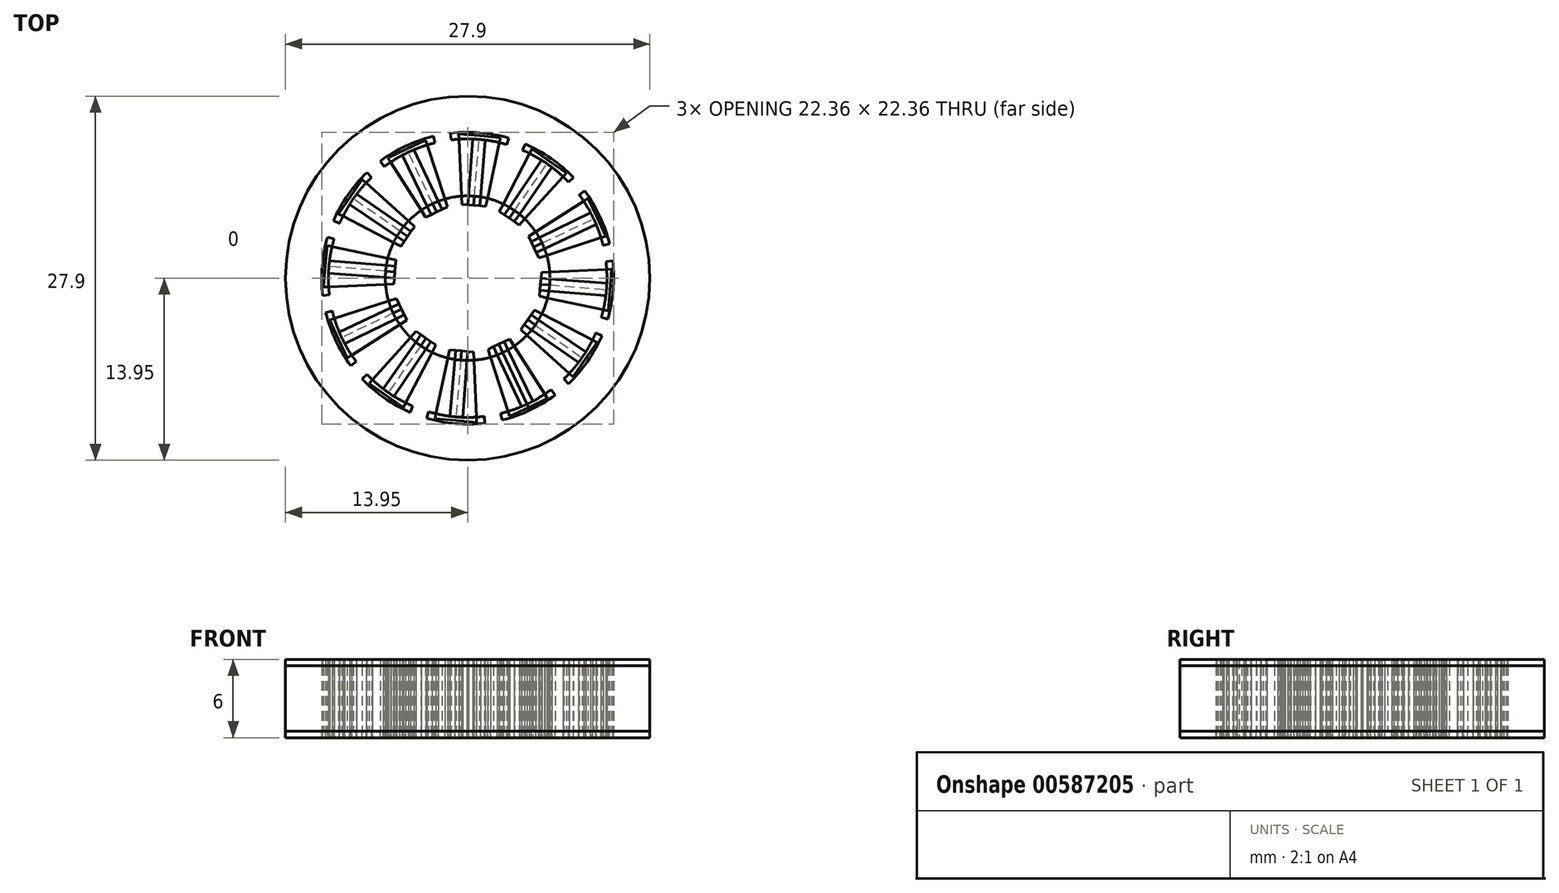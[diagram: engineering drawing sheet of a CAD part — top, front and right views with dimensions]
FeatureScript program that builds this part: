
annotation { "Feature Type Name" : "Feature", "Feature Type Description" : "" }
export const myFeature = defineFeature(function(context is Context, id is Id, definition is map)
    precondition{}
    {
        {
            var Q0;
            Q0=qCreatedBy(makeId("Top.planeOp"),FACE);
            var sketch = newSketch(context, id + "F0", { "sketchPlane" : qUnion([Q0])});
            skCircle(sketch, "E0", {"center": v(0, 0) * mm, "radius": 13.95 * mm});
            skCircle(sketch, "E1", {"center": v(0, 0) * mm, "radius": 4 * mm});
            skCircle(sketch, "E2", {"center": v(0, 0) * mm, "radius": 4.7 * mm});
            skCircle(sketch, "E3", {"center": v(0, 0) * mm, "radius": 6.3 * mm});
            skCircle(sketch, "E4", {"center": v(0, 0) * mm, "radius": 11.19 * mm, "construction": true});
            skCircle(sketch, "E5", {"center": v(0, 0) * mm, "radius": 10.67 * mm, "construction": true});
            skLineSegment(sketch, "E6", {"start": v(0, 0) * mm, "end": v(6.7, -8.96) * mm, "construction": true});
            skLineSegment(sketch, "E7", {"start": v(0, 0) * mm, "end": v(2.64, -10.87) * mm, "construction": true});
            skArc(sketch, "E8", {"start": v(2.52, -10.37) * mm, "mid": v(4.55, -9.65) * mm, "end": v(6.39, -8.54) * mm});
            skArc(sketch, "E9", {"start": v(2.64, -10.87) * mm, "mid": v(4.76, -10.11) * mm, "end": v(6.7, -8.96) * mm});
            skLineSegment(sketch, "E10", {"start": v(6.7, -8.96) * mm, "end": v(6.39, -8.54) * mm});
            skLineSegment(sketch, "E11", {"start": v(2.64, -10.87) * mm, "end": v(2.52, -10.37) * mm});
            skLineSegment(sketch, "E12", {"start": v(0, 0) * mm, "end": v(4.55, -9.65) * mm});
            skLineSegment(sketch, "E13", {"start": v(4.55, -9.65) * mm, "end": v(4.66, -9.9) * mm});
            skLineSegment(sketch, "E14", {"start": v(4.66, -9.9) * mm, "end": v(6.11, -9.22) * mm});
            skLineSegment(sketch, "E15", {"start": v(4.66, -9.9) * mm, "end": v(3.22, -10.58) * mm});
            skLineSegment(sketch, "E16", {"start": v(2.88, -6.12) * mm, "end": v(2.38, -5.06) * mm});
            skLineSegment(sketch, "E17", {"start": v(2.38, -5.06) * mm, "end": v(3.22, -4.67) * mm});
            skLineSegment(sketch, "E18", {"start": v(3.22, -4.67) * mm, "end": v(6.11, -9.22) * mm});
            skLineSegment(sketch, "E19", {"start": v(2.38, -5.06) * mm, "end": v(1.55, -5.45) * mm});
            skLineSegment(sketch, "E20", {"start": v(3.22, -10.58) * mm, "end": v(1.55, -5.45) * mm});
            skLineSegment(sketch, "E21.1.0", {"start": v(0, 0) * mm, "end": v(8.76, -6.08) * mm});
            skLineSegment(sketch, "E21.1.1", {"start": v(0, 0) * mm, "end": v(7.72, -8.1) * mm, "construction": true});
            skLineSegment(sketch, "E21.1.2", {"start": v(0, 0) * mm, "end": v(10.28, -4.4) * mm, "construction": true});
            skLineSegment(sketch, "E21.1.3", {"start": v(4.6, -3.2) * mm, "end": v(5.12, -2.43) * mm});
            skLineSegment(sketch, "E21.1.4", {"start": v(4.6, -3.2) * mm, "end": v(4.07, -3.95) * mm});
            skLineSegment(sketch, "E21.1.5", {"start": v(8.08, -7.56) * mm, "end": v(4.07, -3.95) * mm});
            skLineSegment(sketch, "E21.1.6", {"start": v(5.12, -2.43) * mm, "end": v(9.9, -4.93) * mm});
            skLineSegment(sketch, "E21.1.7", {"start": v(8.99, -6.24) * mm, "end": v(8.08, -7.56) * mm});
            skLineSegment(sketch, "E21.1.8", {"start": v(8.99, -6.24) * mm, "end": v(9.9, -4.93) * mm});
            skArc(sketch, "E21.1.9", {"start": v(7.36, -7.72) * mm, "mid": v(8.76, -6.08) * mm, "end": v(9.8, -4.2) * mm});
            skArc(sketch, "E21.1.10", {"start": v(7.72, -8.1) * mm, "mid": v(9.18, -6.38) * mm, "end": v(10.28, -4.4) * mm});
            skLineSegment(sketch, "E21.2.0", {"start": v(0, 0) * mm, "end": v(10.63, -0.89) * mm});
            skLineSegment(sketch, "E21.2.1", {"start": v(0, 0) * mm, "end": v(10.74, -3.15) * mm, "construction": true});
            skLineSegment(sketch, "E21.2.2", {"start": v(0, 0) * mm, "end": v(11.11, 1.32) * mm, "construction": true});
            skLineSegment(sketch, "E21.2.3", {"start": v(5.58, -0.47) * mm, "end": v(5.65, 0.45) * mm});
            skLineSegment(sketch, "E21.2.4", {"start": v(5.58, -0.47) * mm, "end": v(5.5, -1.38) * mm});
            skLineSegment(sketch, "E21.2.5", {"start": v(10.77, -2.5) * mm, "end": v(5.5, -1.38) * mm});
            skLineSegment(sketch, "E21.2.6", {"start": v(5.65, 0.45) * mm, "end": v(11.04, 0.68) * mm});
            skLineSegment(sketch, "E21.2.7", {"start": v(10.9, -0.91) * mm, "end": v(10.77, -2.5) * mm});
            skLineSegment(sketch, "E21.2.8", {"start": v(10.9, -0.91) * mm, "end": v(11.04, 0.68) * mm});
            skArc(sketch, "E21.2.9", {"start": v(10.24, -3) * mm, "mid": v(10.63, -0.89) * mm, "end": v(10.6, 1.26) * mm});
            skArc(sketch, "E21.2.10", {"start": v(10.74, -3.15) * mm, "mid": v(11.14, -0.93) * mm, "end": v(11.11, 1.32) * mm});
            skLineSegment(sketch, "E21.3.0", {"start": v(0, 0) * mm, "end": v(9.65, 4.55) * mm});
            skLineSegment(sketch, "E21.3.1", {"start": v(0, 0) * mm, "end": v(10.87, 2.64) * mm, "construction": true});
            skLineSegment(sketch, "E21.3.2", {"start": v(0, 0) * mm, "end": v(8.96, 6.7) * mm, "construction": true});
            skLineSegment(sketch, "E21.3.3", {"start": v(5.06, 2.38) * mm, "end": v(4.67, 3.22) * mm});
            skLineSegment(sketch, "E21.3.4", {"start": v(5.06, 2.38) * mm, "end": v(5.45, 1.55) * mm});
            skLineSegment(sketch, "E21.3.5", {"start": v(10.58, 3.22) * mm, "end": v(5.45, 1.55) * mm});
            skLineSegment(sketch, "E21.3.6", {"start": v(4.67, 3.22) * mm, "end": v(9.22, 6.11) * mm});
            skLineSegment(sketch, "E21.3.7", {"start": v(9.9, 4.66) * mm, "end": v(10.58, 3.22) * mm});
            skLineSegment(sketch, "E21.3.8", {"start": v(9.9, 4.66) * mm, "end": v(9.22, 6.11) * mm});
            skArc(sketch, "E21.3.9", {"start": v(10.37, 2.52) * mm, "mid": v(9.65, 4.55) * mm, "end": v(8.54, 6.39) * mm});
            skArc(sketch, "E21.3.10", {"start": v(10.87, 2.64) * mm, "mid": v(10.11, 4.76) * mm, "end": v(8.96, 6.7) * mm});
            skLineSegment(sketch, "E21.4.0", {"start": v(0, 0) * mm, "end": v(6.08, 8.76) * mm});
            skLineSegment(sketch, "E21.4.1", {"start": v(0, 0) * mm, "end": v(8.1, 7.72) * mm, "construction": true});
            skLineSegment(sketch, "E21.4.2", {"start": v(0, 0) * mm, "end": v(4.4, 10.28) * mm, "construction": true});
            skLineSegment(sketch, "E21.4.3", {"start": v(3.2, 4.6) * mm, "end": v(2.43, 5.12) * mm});
            skLineSegment(sketch, "E21.4.4", {"start": v(3.2, 4.6) * mm, "end": v(3.95, 4.07) * mm});
            skLineSegment(sketch, "E21.4.5", {"start": v(7.56, 8.08) * mm, "end": v(3.95, 4.07) * mm});
            skLineSegment(sketch, "E21.4.6", {"start": v(2.43, 5.12) * mm, "end": v(4.93, 9.9) * mm});
            skLineSegment(sketch, "E21.4.7", {"start": v(6.24, 8.99) * mm, "end": v(7.56, 8.08) * mm});
            skLineSegment(sketch, "E21.4.8", {"start": v(6.24, 8.99) * mm, "end": v(4.93, 9.9) * mm});
            skArc(sketch, "E21.4.9", {"start": v(7.72, 7.36) * mm, "mid": v(6.08, 8.76) * mm, "end": v(4.2, 9.8) * mm});
            skArc(sketch, "E21.4.10", {"start": v(8.1, 7.72) * mm, "mid": v(6.38, 9.18) * mm, "end": v(4.4, 10.28) * mm});
            skLineSegment(sketch, "E21.5.0", {"start": v(0, 0) * mm, "end": v(0.89, 10.63) * mm});
            skLineSegment(sketch, "E21.5.1", {"start": v(0, 0) * mm, "end": v(3.15, 10.74) * mm, "construction": true});
            skLineSegment(sketch, "E21.5.2", {"start": v(0, 0) * mm, "end": v(-1.32, 11.11) * mm, "construction": true});
            skLineSegment(sketch, "E21.5.3", {"start": v(0.47, 5.58) * mm, "end": v(-0.45, 5.65) * mm});
            skLineSegment(sketch, "E21.5.4", {"start": v(0.47, 5.58) * mm, "end": v(1.38, 5.5) * mm});
            skLineSegment(sketch, "E21.5.5", {"start": v(2.5, 10.77) * mm, "end": v(1.38, 5.5) * mm});
            skLineSegment(sketch, "E21.5.6", {"start": v(-0.45, 5.65) * mm, "end": v(-0.68, 11.04) * mm});
            skLineSegment(sketch, "E21.5.7", {"start": v(0.91, 10.9) * mm, "end": v(2.5, 10.77) * mm});
            skLineSegment(sketch, "E21.5.8", {"start": v(0.91, 10.9) * mm, "end": v(-0.68, 11.04) * mm});
            skArc(sketch, "E21.5.9", {"start": v(3, 10.24) * mm, "mid": v(0.89, 10.63) * mm, "end": v(-1.26, 10.6) * mm});
            skArc(sketch, "E21.5.10", {"start": v(3.15, 10.74) * mm, "mid": v(0.93, 11.14) * mm, "end": v(-1.32, 11.11) * mm});
            skLineSegment(sketch, "E21.6.0", {"start": v(0, 0) * mm, "end": v(-4.55, 9.65) * mm});
            skLineSegment(sketch, "E21.6.1", {"start": v(0, 0) * mm, "end": v(-2.64, 10.87) * mm, "construction": true});
            skLineSegment(sketch, "E21.6.2", {"start": v(0, 0) * mm, "end": v(-6.7, 8.96) * mm, "construction": true});
            skLineSegment(sketch, "E21.6.3", {"start": v(-2.38, 5.06) * mm, "end": v(-3.22, 4.67) * mm});
            skLineSegment(sketch, "E21.6.4", {"start": v(-2.38, 5.06) * mm, "end": v(-1.55, 5.45) * mm});
            skLineSegment(sketch, "E21.6.5", {"start": v(-3.22, 10.58) * mm, "end": v(-1.55, 5.45) * mm});
            skLineSegment(sketch, "E21.6.6", {"start": v(-3.22, 4.67) * mm, "end": v(-6.11, 9.22) * mm});
            skLineSegment(sketch, "E21.6.7", {"start": v(-4.66, 9.9) * mm, "end": v(-3.22, 10.58) * mm});
            skLineSegment(sketch, "E21.6.8", {"start": v(-4.66, 9.9) * mm, "end": v(-6.11, 9.22) * mm});
            skArc(sketch, "E21.6.9", {"start": v(-2.52, 10.37) * mm, "mid": v(-4.55, 9.65) * mm, "end": v(-6.39, 8.54) * mm});
            skArc(sketch, "E21.6.10", {"start": v(-2.64, 10.87) * mm, "mid": v(-4.76, 10.11) * mm, "end": v(-6.7, 8.96) * mm});
            skLineSegment(sketch, "E21.7.0", {"start": v(0, 0) * mm, "end": v(-8.76, 6.08) * mm});
            skLineSegment(sketch, "E21.7.1", {"start": v(0, 0) * mm, "end": v(-7.72, 8.1) * mm, "construction": true});
            skLineSegment(sketch, "E21.7.2", {"start": v(0, 0) * mm, "end": v(-10.28, 4.4) * mm, "construction": true});
            skLineSegment(sketch, "E21.7.3", {"start": v(-4.6, 3.2) * mm, "end": v(-5.12, 2.43) * mm});
            skLineSegment(sketch, "E21.7.4", {"start": v(-4.6, 3.2) * mm, "end": v(-4.07, 3.95) * mm});
            skLineSegment(sketch, "E21.7.5", {"start": v(-8.08, 7.56) * mm, "end": v(-4.07, 3.95) * mm});
            skLineSegment(sketch, "E21.7.6", {"start": v(-5.12, 2.43) * mm, "end": v(-9.9, 4.93) * mm});
            skLineSegment(sketch, "E21.7.7", {"start": v(-8.99, 6.24) * mm, "end": v(-8.08, 7.56) * mm});
            skLineSegment(sketch, "E21.7.8", {"start": v(-8.99, 6.24) * mm, "end": v(-9.9, 4.93) * mm});
            skArc(sketch, "E21.7.9", {"start": v(-7.36, 7.72) * mm, "mid": v(-8.76, 6.08) * mm, "end": v(-9.8, 4.2) * mm});
            skArc(sketch, "E21.7.10", {"start": v(-7.72, 8.1) * mm, "mid": v(-9.18, 6.38) * mm, "end": v(-10.28, 4.4) * mm});
            skLineSegment(sketch, "E21.8.0", {"start": v(0, 0) * mm, "end": v(-10.63, 0.89) * mm});
            skLineSegment(sketch, "E21.8.1", {"start": v(0, 0) * mm, "end": v(-10.74, 3.15) * mm, "construction": true});
            skLineSegment(sketch, "E21.8.2", {"start": v(0, 0) * mm, "end": v(-11.11, -1.32) * mm, "construction": true});
            skLineSegment(sketch, "E21.8.3", {"start": v(-5.58, 0.47) * mm, "end": v(-5.65, -0.45) * mm});
            skLineSegment(sketch, "E21.8.4", {"start": v(-5.58, 0.47) * mm, "end": v(-5.5, 1.38) * mm});
            skLineSegment(sketch, "E21.8.5", {"start": v(-10.77, 2.5) * mm, "end": v(-5.5, 1.38) * mm});
            skLineSegment(sketch, "E21.8.6", {"start": v(-5.65, -0.45) * mm, "end": v(-11.04, -0.68) * mm});
            skLineSegment(sketch, "E21.8.7", {"start": v(-10.9, 0.91) * mm, "end": v(-10.77, 2.5) * mm});
            skLineSegment(sketch, "E21.8.8", {"start": v(-10.9, 0.91) * mm, "end": v(-11.04, -0.68) * mm});
            skArc(sketch, "E21.8.9", {"start": v(-10.24, 3) * mm, "mid": v(-10.63, 0.89) * mm, "end": v(-10.6, -1.26) * mm});
            skArc(sketch, "E21.8.10", {"start": v(-10.74, 3.15) * mm, "mid": v(-11.14, 0.93) * mm, "end": v(-11.11, -1.32) * mm});
            skLineSegment(sketch, "E21.9.0", {"start": v(0, 0) * mm, "end": v(-9.65, -4.55) * mm});
            skLineSegment(sketch, "E21.9.1", {"start": v(0, 0) * mm, "end": v(-10.87, -2.64) * mm, "construction": true});
            skLineSegment(sketch, "E21.9.2", {"start": v(0, 0) * mm, "end": v(-8.96, -6.7) * mm, "construction": true});
            skLineSegment(sketch, "E21.9.3", {"start": v(-5.06, -2.38) * mm, "end": v(-4.67, -3.22) * mm});
            skLineSegment(sketch, "E21.9.4", {"start": v(-5.06, -2.38) * mm, "end": v(-5.45, -1.55) * mm});
            skLineSegment(sketch, "E21.9.5", {"start": v(-10.58, -3.22) * mm, "end": v(-5.45, -1.55) * mm});
            skLineSegment(sketch, "E21.9.6", {"start": v(-4.67, -3.22) * mm, "end": v(-9.22, -6.11) * mm});
            skLineSegment(sketch, "E21.9.7", {"start": v(-9.9, -4.66) * mm, "end": v(-10.58, -3.22) * mm});
            skLineSegment(sketch, "E21.9.8", {"start": v(-9.9, -4.66) * mm, "end": v(-9.22, -6.11) * mm});
            skArc(sketch, "E21.9.9", {"start": v(-10.37, -2.52) * mm, "mid": v(-9.65, -4.55) * mm, "end": v(-8.54, -6.39) * mm});
            skArc(sketch, "E21.9.10", {"start": v(-10.87, -2.64) * mm, "mid": v(-10.11, -4.76) * mm, "end": v(-8.96, -6.7) * mm});
            skLineSegment(sketch, "E21.10.0", {"start": v(0, 0) * mm, "end": v(-6.08, -8.76) * mm});
            skLineSegment(sketch, "E21.10.1", {"start": v(0, 0) * mm, "end": v(-8.1, -7.72) * mm, "construction": true});
            skLineSegment(sketch, "E21.10.2", {"start": v(0, 0) * mm, "end": v(-4.4, -10.28) * mm, "construction": true});
            skLineSegment(sketch, "E21.10.3", {"start": v(-3.2, -4.6) * mm, "end": v(-2.43, -5.12) * mm});
            skLineSegment(sketch, "E21.10.4", {"start": v(-3.2, -4.6) * mm, "end": v(-3.95, -4.07) * mm});
            skLineSegment(sketch, "E21.10.5", {"start": v(-7.56, -8.08) * mm, "end": v(-3.95, -4.07) * mm});
            skLineSegment(sketch, "E21.10.6", {"start": v(-2.43, -5.12) * mm, "end": v(-4.93, -9.9) * mm});
            skLineSegment(sketch, "E21.10.7", {"start": v(-6.24, -8.99) * mm, "end": v(-7.56, -8.08) * mm});
            skLineSegment(sketch, "E21.10.8", {"start": v(-6.24, -8.99) * mm, "end": v(-4.93, -9.9) * mm});
            skArc(sketch, "E21.10.9", {"start": v(-7.72, -7.36) * mm, "mid": v(-6.08, -8.76) * mm, "end": v(-4.2, -9.8) * mm});
            skArc(sketch, "E21.10.10", {"start": v(-8.1, -7.72) * mm, "mid": v(-6.38, -9.18) * mm, "end": v(-4.4, -10.28) * mm});
            skLineSegment(sketch, "E21.11.0", {"start": v(0, 0) * mm, "end": v(-0.89, -10.63) * mm});
            skLineSegment(sketch, "E21.11.1", {"start": v(0, 0) * mm, "end": v(-3.15, -10.74) * mm, "construction": true});
            skLineSegment(sketch, "E21.11.2", {"start": v(0, 0) * mm, "end": v(1.32, -11.11) * mm, "construction": true});
            skLineSegment(sketch, "E21.11.3", {"start": v(-0.47, -5.58) * mm, "end": v(0.45, -5.65) * mm});
            skLineSegment(sketch, "E21.11.4", {"start": v(-0.47, -5.58) * mm, "end": v(-1.38, -5.5) * mm});
            skLineSegment(sketch, "E21.11.5", {"start": v(-2.5, -10.77) * mm, "end": v(-1.38, -5.5) * mm});
            skLineSegment(sketch, "E21.11.6", {"start": v(0.45, -5.65) * mm, "end": v(0.68, -11.04) * mm});
            skLineSegment(sketch, "E21.11.7", {"start": v(-0.91, -10.9) * mm, "end": v(-2.5, -10.77) * mm});
            skLineSegment(sketch, "E21.11.8", {"start": v(-0.91, -10.9) * mm, "end": v(0.68, -11.04) * mm});
            skArc(sketch, "E21.11.9", {"start": v(-3, -10.24) * mm, "mid": v(-0.89, -10.63) * mm, "end": v(1.26, -10.6) * mm});
            skArc(sketch, "E21.11.10", {"start": v(-3.15, -10.74) * mm, "mid": v(-0.93, -11.14) * mm, "end": v(1.32, -11.11) * mm});
            skLineSegment(sketch, "E22", {"start": v(0, 0) * mm, "end": v(15.73, -14.85) * mm, "construction": true});
            skLineSegment(sketch, "E23", {"start": v(1.32, -11.11) * mm, "end": v(1.26, -10.6) * mm});
            skLineSegment(sketch, "E24", {"start": v(-3.15, -10.74) * mm, "end": v(-3, -10.24) * mm});
            skLineSegment(sketch, "E25", {"start": v(-4.4, -10.28) * mm, "end": v(-4.2, -9.8) * mm});
            skLineSegment(sketch, "E26", {"start": v(7.72, -8.1) * mm, "end": v(7.36, -7.72) * mm});
            skLineSegment(sketch, "E27", {"start": v(10.28, -4.4) * mm, "end": v(9.8, -4.2) * mm});
            skLineSegment(sketch, "E28", {"start": v(10.74, -3.15) * mm, "end": v(10.24, -3) * mm});
            skLineSegment(sketch, "E29", {"start": v(11.11, 1.32) * mm, "end": v(10.6, 1.26) * mm});
            skLineSegment(sketch, "E30", {"start": v(-8.1, -7.72) * mm, "end": v(-7.72, -7.36) * mm});
            skLineSegment(sketch, "E31", {"start": v(-8.96, -6.7) * mm, "end": v(-8.54, -6.39) * mm});
            skLineSegment(sketch, "E32", {"start": v(-10.87, -2.64) * mm, "end": v(-10.37, -2.52) * mm});
            skLineSegment(sketch, "E33", {"start": v(-11.11, -1.32) * mm, "end": v(-10.6, -1.26) * mm});
            skLineSegment(sketch, "E34", {"start": v(-10.74, 3.15) * mm, "end": v(-10.24, 3) * mm});
            skLineSegment(sketch, "E35", {"start": v(-10.28, 4.4) * mm, "end": v(-9.8, 4.2) * mm});
            skLineSegment(sketch, "E36", {"start": v(-7.72, 8.1) * mm, "end": v(-7.36, 7.72) * mm});
            skLineSegment(sketch, "E37", {"start": v(-6.7, 8.96) * mm, "end": v(-6.39, 8.54) * mm});
            skLineSegment(sketch, "E38", {"start": v(-2.64, 10.87) * mm, "end": v(-2.52, 10.37) * mm});
            skLineSegment(sketch, "E39", {"start": v(-1.32, 11.11) * mm, "end": v(-1.26, 10.6) * mm});
            skLineSegment(sketch, "E40", {"start": v(3.15, 10.74) * mm, "end": v(3, 10.24) * mm});
            skLineSegment(sketch, "E41", {"start": v(4.2, 9.8) * mm, "end": v(4.4, 10.28) * mm});
            skLineSegment(sketch, "E42", {"start": v(7.72, 7.36) * mm, "end": v(8.1, 7.72) * mm});
            skLineSegment(sketch, "E43", {"start": v(8.54, 6.39) * mm, "end": v(8.96, 6.7) * mm});
            skLineSegment(sketch, "E44", {"start": v(10.37, 2.52) * mm, "end": v(10.87, 2.64) * mm});
            skLineSegment(sketch, "E45", {"start": v(1.97, -5.26) * mm, "end": v(4.13, -9.84) * mm});
            skLineSegment(sketch, "E46", {"start": v(2.8, -4.86) * mm, "end": v(5, -9.42) * mm});
            skLineSegment(sketch, "E47.1.0", {"start": v(4.33, -3.57) * mm, "end": v(8.5, -6.46) * mm});
            skLineSegment(sketch, "E47.1.1", {"start": v(4.86, -2.81) * mm, "end": v(9.04, -5.65) * mm});
            skLineSegment(sketch, "E47.2.0", {"start": v(5.54, -0.92) * mm, "end": v(10.58, -1.35) * mm});
            skLineSegment(sketch, "E47.2.1", {"start": v(5.61, 0) * mm, "end": v(10.66, -0.37) * mm});
            skLineSegment(sketch, "E47.3.0", {"start": v(5.26, 1.97) * mm, "end": v(9.84, 4.13) * mm});
            skLineSegment(sketch, "E47.3.1", {"start": v(4.86, 2.8) * mm, "end": v(9.42, 5) * mm});
            skLineSegment(sketch, "E47.4.0", {"start": v(3.57, 4.33) * mm, "end": v(6.46, 8.5) * mm});
            skLineSegment(sketch, "E47.4.1", {"start": v(2.81, 4.86) * mm, "end": v(5.65, 9.04) * mm});
            skLineSegment(sketch, "E47.5.0", {"start": v(0.92, 5.54) * mm, "end": v(1.35, 10.58) * mm});
            skLineSegment(sketch, "E47.5.1", {"start": v(0, 5.61) * mm, "end": v(0.37, 10.66) * mm});
            skLineSegment(sketch, "E47.6.0", {"start": v(-1.97, 5.26) * mm, "end": v(-4.13, 9.84) * mm});
            skLineSegment(sketch, "E47.6.1", {"start": v(-2.8, 4.86) * mm, "end": v(-5, 9.42) * mm});
            skLineSegment(sketch, "E47.7.0", {"start": v(-4.33, 3.57) * mm, "end": v(-8.5, 6.46) * mm});
            skLineSegment(sketch, "E47.7.1", {"start": v(-4.86, 2.81) * mm, "end": v(-9.04, 5.65) * mm});
            skLineSegment(sketch, "E47.8.0", {"start": v(-5.54, 0.92) * mm, "end": v(-10.58, 1.35) * mm});
            skLineSegment(sketch, "E47.8.1", {"start": v(-5.61, 0) * mm, "end": v(-10.66, 0.37) * mm});
            skLineSegment(sketch, "E47.9.0", {"start": v(-5.26, -1.97) * mm, "end": v(-9.84, -4.13) * mm});
            skLineSegment(sketch, "E47.9.1", {"start": v(-4.86, -2.8) * mm, "end": v(-9.42, -5) * mm});
            skLineSegment(sketch, "E47.10.0", {"start": v(-3.57, -4.33) * mm, "end": v(-6.46, -8.5) * mm});
            skLineSegment(sketch, "E47.10.1", {"start": v(-2.81, -4.86) * mm, "end": v(-5.65, -9.04) * mm});
            skLineSegment(sketch, "E47.11.0", {"start": v(-0.92, -5.54) * mm, "end": v(-1.35, -10.58) * mm});
            skLineSegment(sketch, "E47.11.1", {"start": v(0, -5.61) * mm, "end": v(-0.37, -10.66) * mm});
            skArc(sketch, "E48", {"start": v(-4.4, -1.63) * mm, "mid": v(-4.6, -2.17) * mm, "end": v(-4.06, -2.35) * mm});
            skSolve(sketch);
        }
        {
            var Q0;
            Q0=makeQuery(id+"F0.imprint","IMPRINT",FACE,{"disambiguationData":[TD([[makeQuery(id+"F0.imprint","IMPRINT",EDGE,{"derivedFrom":sQuery(id+"F0.wireOp",EDGE,"E9")}),1.0]])]});
            var Q1;
            {var subQ0=sQuery(id+"F0.wireOp",EDGE,"E13");Q1=makeQuery(id+"F0.imprint","IMPRINT",FACE,{"disambiguationData":[TD([[makeQuery(id+"F0.imprint","IMPRINT",EDGE,{"derivedFrom":subQ0}),1.0]])]});}
            var Q2;
            {var subQ0=sQuery(id+"F0.wireOp",EDGE,"E13");Q2=makeQuery(id+"F0.imprint","IMPRINT",FACE,{"disambiguationData":[TD([[makeQuery(id+"F0.imprint","IMPRINT",EDGE,{"derivedFrom":subQ0}),-1.0]])]});}
            var Q3;
            {var subQ1=sQuery(id+"F0.wireOp",EDGE,"E21.11.7");Q3=makeQuery(id+"F0.imprint","IMPRINT",FACE,{"disambiguationData":[TD([[makeQuery(id+"F0.imprint","IMPRINT",EDGE,{"derivedFrom":subQ1}),1.0]])]});}
            var Q4;
            {var subQ1=sQuery(id+"F0.wireOp",EDGE,"E21.11.7");Q4=makeQuery(id+"F0.imprint","IMPRINT",FACE,{"disambiguationData":[TD([[makeQuery(id+"F0.imprint","IMPRINT",EDGE,{"derivedFrom":subQ1}),-1.0]])]});}
            var Q5;
            {var subQ2=sQuery(id+"F0.wireOp",EDGE,"E21.10.7");Q5=makeQuery(id+"F0.imprint","IMPRINT",FACE,{"disambiguationData":[TD([[makeQuery(id+"F0.imprint","IMPRINT",EDGE,{"derivedFrom":subQ2}),1.0]])]});}
            var Q6;
            {var subQ1=sQuery(id+"F0.wireOp",EDGE,"E21.10.7");Q6=makeQuery(id+"F0.imprint","IMPRINT",FACE,{"disambiguationData":[TD([[makeQuery(id+"F0.imprint","IMPRINT",EDGE,{"derivedFrom":subQ1}),-1.0]])]});}
            var Q7;
            {var subQ2=sQuery(id+"F0.wireOp",EDGE,"E21.9.7");Q7=makeQuery(id+"F0.imprint","IMPRINT",FACE,{"disambiguationData":[TD([[makeQuery(id+"F0.imprint","IMPRINT",EDGE,{"derivedFrom":subQ2}),1.0]])]});}
            var Q8;
            {var subQ1=sQuery(id+"F0.wireOp",EDGE,"E21.9.7");Q8=makeQuery(id+"F0.imprint","IMPRINT",FACE,{"disambiguationData":[TD([[makeQuery(id+"F0.imprint","IMPRINT",EDGE,{"derivedFrom":subQ1}),-1.0]])]});}
            var Q9;
            {var subQ2=sQuery(id+"F0.wireOp",EDGE,"E21.8.7");Q9=makeQuery(id+"F0.imprint","IMPRINT",FACE,{"disambiguationData":[TD([[makeQuery(id+"F0.imprint","IMPRINT",EDGE,{"derivedFrom":subQ2}),1.0]])]});}
            var Q10;
            {var subQ1=sQuery(id+"F0.wireOp",EDGE,"E21.8.7");Q10=makeQuery(id+"F0.imprint","IMPRINT",FACE,{"disambiguationData":[TD([[makeQuery(id+"F0.imprint","IMPRINT",EDGE,{"derivedFrom":subQ1}),-1.0]])]});}
            var Q11;
            {var subQ1=sQuery(id+"F0.wireOp",EDGE,"E21.1.7");Q11=makeQuery(id+"F0.imprint","IMPRINT",FACE,{"disambiguationData":[TD([[makeQuery(id+"F0.imprint","IMPRINT",EDGE,{"derivedFrom":subQ1}),1.0]])]});}
            var Q12;
            {var subQ1=sQuery(id+"F0.wireOp",EDGE,"E21.1.7");Q12=makeQuery(id+"F0.imprint","IMPRINT",FACE,{"disambiguationData":[TD([[makeQuery(id+"F0.imprint","IMPRINT",EDGE,{"derivedFrom":subQ1}),-1.0]])]});}
            var Q13;
            {var subQ1=sQuery(id+"F0.wireOp",EDGE,"E21.2.7");Q13=makeQuery(id+"F0.imprint","IMPRINT",FACE,{"disambiguationData":[TD([[makeQuery(id+"F0.imprint","IMPRINT",EDGE,{"derivedFrom":subQ1}),1.0]])]});}
            var Q14;
            {var subQ1=sQuery(id+"F0.wireOp",EDGE,"E21.2.7");Q14=makeQuery(id+"F0.imprint","IMPRINT",FACE,{"disambiguationData":[TD([[makeQuery(id+"F0.imprint","IMPRINT",EDGE,{"derivedFrom":subQ1}),-1.0]])]});}
            var Q15;
            {var subQ2=sQuery(id+"F0.wireOp",EDGE,"E21.3.7");Q15=makeQuery(id+"F0.imprint","IMPRINT",FACE,{"disambiguationData":[TD([[makeQuery(id+"F0.imprint","IMPRINT",EDGE,{"derivedFrom":subQ2}),1.0]])]});}
            var Q16;
            {var subQ1=sQuery(id+"F0.wireOp",EDGE,"E21.3.7");Q16=makeQuery(id+"F0.imprint","IMPRINT",FACE,{"disambiguationData":[TD([[makeQuery(id+"F0.imprint","IMPRINT",EDGE,{"derivedFrom":subQ1}),-1.0]])]});}
            var Q17;
            {var subQ2=sQuery(id+"F0.wireOp",EDGE,"E21.4.7");Q17=makeQuery(id+"F0.imprint","IMPRINT",FACE,{"disambiguationData":[TD([[makeQuery(id+"F0.imprint","IMPRINT",EDGE,{"derivedFrom":subQ2}),1.0]])]});}
            var Q18;
            {var subQ1=sQuery(id+"F0.wireOp",EDGE,"E21.4.7");Q18=makeQuery(id+"F0.imprint","IMPRINT",FACE,{"disambiguationData":[TD([[makeQuery(id+"F0.imprint","IMPRINT",EDGE,{"derivedFrom":subQ1}),-1.0]])]});}
            var Q19;
            {var subQ2=sQuery(id+"F0.wireOp",EDGE,"E21.5.7");Q19=makeQuery(id+"F0.imprint","IMPRINT",FACE,{"disambiguationData":[TD([[makeQuery(id+"F0.imprint","IMPRINT",EDGE,{"derivedFrom":subQ2}),1.0]])]});}
            var Q20;
            {var subQ1=sQuery(id+"F0.wireOp",EDGE,"E21.5.7");Q20=makeQuery(id+"F0.imprint","IMPRINT",FACE,{"disambiguationData":[TD([[makeQuery(id+"F0.imprint","IMPRINT",EDGE,{"derivedFrom":subQ1}),-1.0]])]});}
            var Q21;
            {var subQ2=sQuery(id+"F0.wireOp",EDGE,"E21.6.7");Q21=makeQuery(id+"F0.imprint","IMPRINT",FACE,{"disambiguationData":[TD([[makeQuery(id+"F0.imprint","IMPRINT",EDGE,{"derivedFrom":subQ2}),1.0]])]});}
            var Q22;
            {var subQ1=sQuery(id+"F0.wireOp",EDGE,"E21.6.7");Q22=makeQuery(id+"F0.imprint","IMPRINT",FACE,{"disambiguationData":[TD([[makeQuery(id+"F0.imprint","IMPRINT",EDGE,{"derivedFrom":subQ1}),-1.0]])]});}
            var Q23;
            {var subQ2=sQuery(id+"F0.wireOp",EDGE,"E21.7.7");Q23=makeQuery(id+"F0.imprint","IMPRINT",FACE,{"disambiguationData":[TD([[makeQuery(id+"F0.imprint","IMPRINT",EDGE,{"derivedFrom":subQ2}),1.0]])]});}
            var Q24;
            {var subQ1=sQuery(id+"F0.wireOp",EDGE,"E21.7.7");Q24=makeQuery(id+"F0.imprint","IMPRINT",FACE,{"disambiguationData":[TD([[makeQuery(id+"F0.imprint","IMPRINT",EDGE,{"derivedFrom":subQ1}),-1.0]])]});}
            var Q25;
            {var subQ0=sQuery(id+"F0.wireOp",EDGE,"E21.7.3");Q25=makeQuery(id+"F0.imprint","IMPRINT",FACE,{"disambiguationData":[TD([[makeQuery(id+"F0.imprint","IMPRINT",EDGE,{"derivedFrom":subQ0}),1.0]])]});}
            var Q26;
            {var subQ10=sQuery(id+"F0.wireOp",EDGE,"E21.9.3");Q26=makeQuery(id+"F0.imprint","IMPRINT",FACE,{"disambiguationData":[TD([[makeQuery(id+"F0.imprint","IMPRINT",EDGE,{"derivedFrom":subQ10}),1.0]])]});}
            var Q27;
            {var subQ0=sQuery(id+"F0.wireOp",EDGE,"E21.10.3");Q27=makeQuery(id+"F0.imprint","IMPRINT",FACE,{"disambiguationData":[TD([[makeQuery(id+"F0.imprint","IMPRINT",EDGE,{"derivedFrom":subQ0}),1.0]])]});}
            var Q28;
            {var subQ0=sQuery(id+"F0.wireOp",EDGE,"E19");Q28=makeQuery(id+"F0.imprint","IMPRINT",FACE,{"disambiguationData":[TD([[makeQuery(id+"F0.imprint","IMPRINT",EDGE,{"derivedFrom":subQ0}),-1.0]])]});}
            var Q29;
            {var subQ0=sQuery(id+"F0.wireOp",EDGE,"E17");Q29=makeQuery(id+"F0.imprint","IMPRINT",FACE,{"disambiguationData":[TD([[makeQuery(id+"F0.imprint","IMPRINT",EDGE,{"derivedFrom":subQ0}),1.0]])]});}
            var Q30;
            {var subQ0=sQuery(id+"F0.wireOp",EDGE,"E21.1.3");Q30=makeQuery(id+"F0.imprint","IMPRINT",FACE,{"disambiguationData":[TD([[makeQuery(id+"F0.imprint","IMPRINT",EDGE,{"derivedFrom":subQ0}),1.0]])]});}
            var Q31;
            {var subQ0=sQuery(id+"F0.wireOp",EDGE,"E21.2.3");Q31=makeQuery(id+"F0.imprint","IMPRINT",FACE,{"disambiguationData":[TD([[makeQuery(id+"F0.imprint","IMPRINT",EDGE,{"derivedFrom":subQ0}),1.0]])]});}
            var Q32;
            {var subQ0=sQuery(id+"F0.wireOp",EDGE,"E21.3.3");Q32=makeQuery(id+"F0.imprint","IMPRINT",FACE,{"disambiguationData":[TD([[makeQuery(id+"F0.imprint","IMPRINT",EDGE,{"derivedFrom":subQ0}),1.0]])]});}
            var Q33;
            {var subQ0=sQuery(id+"F0.wireOp",EDGE,"E21.4.3");Q33=makeQuery(id+"F0.imprint","IMPRINT",FACE,{"disambiguationData":[TD([[makeQuery(id+"F0.imprint","IMPRINT",EDGE,{"derivedFrom":subQ0}),1.0]])]});}
            var Q34;
            {var subQ0=sQuery(id+"F0.wireOp",EDGE,"E21.5.3");Q34=makeQuery(id+"F0.imprint","IMPRINT",FACE,{"disambiguationData":[TD([[makeQuery(id+"F0.imprint","IMPRINT",EDGE,{"derivedFrom":subQ0}),1.0]])]});}
            var Q35;
            {var subQ0=sQuery(id+"F0.wireOp",EDGE,"E21.6.3");Q35=makeQuery(id+"F0.imprint","IMPRINT",FACE,{"disambiguationData":[TD([[makeQuery(id+"F0.imprint","IMPRINT",EDGE,{"derivedFrom":subQ0}),1.0]])]});}
            var Q36;
            {var subQ0=sQuery(id+"F0.wireOp",EDGE,"E21.8.3");Q36=makeQuery(id+"F0.imprint","IMPRINT",FACE,{"disambiguationData":[TD([[makeQuery(id+"F0.imprint","IMPRINT",EDGE,{"derivedFrom":subQ0}),1.0]])]});}
            var Q37;
            {var subQ3=sQuery(id+"F0.wireOp",EDGE,"E3");var subQ7=sQuery(id+"F0.wireOp",EDGE,"E45");var subQ8=makeQuery(id+"F0.imprint","INTERSECT",VERTEX,{"derivedFrom":[subQ3,subQ7]});Q37=makeQuery(id+"F0.imprint","IMPRINT",FACE,{"disambiguationData":[TD([[makeQuery(id+"F0.imprint","IMPRINT",EDGE,{"disambiguationData":[TD([[subQ8,-1.0]])],"derivedFrom":subQ3}),-1.0]])]});}
            var Q38;
            {var subQ3=sQuery(id+"F0.wireOp",EDGE,"E16");var subQ7=sQuery(id+"F0.wireOp",EDGE,"E3");var subQ8=makeQuery(id+"F0.imprint","INTERSECT",VERTEX,{"derivedFrom":[subQ7,subQ3]});Q38=makeQuery(id+"F0.imprint","IMPRINT",FACE,{"disambiguationData":[TD([[makeQuery(id+"F0.imprint","IMPRINT",EDGE,{"disambiguationData":[TD([[subQ8,-1.0]])],"derivedFrom":subQ7}),-1.0]])]});}
            var Q39;
            {var subQ0=sQuery(id+"F0.wireOp",EDGE,"E20");var subQ1=sQuery(id+"F0.wireOp",EDGE,"E3");var subQ2=makeQuery(id+"F0.imprint","INTERSECT",VERTEX,{"derivedFrom":[subQ1,subQ0]});Q39=makeQuery(id+"F0.imprint","IMPRINT",FACE,{"disambiguationData":[TD([[makeQuery(id+"F0.imprint","IMPRINT",EDGE,{"disambiguationData":[TD([[subQ2,-1.0]])],"derivedFrom":subQ1}),1.0]])]});}
            var Q40;
            {var subQ0=sQuery(id+"F0.wireOp",EDGE,"E45");var subQ1=sQuery(id+"F0.wireOp",EDGE,"E3");var subQ2=makeQuery(id+"F0.imprint","INTERSECT",VERTEX,{"derivedFrom":[subQ1,subQ0]});Q40=makeQuery(id+"F0.imprint","IMPRINT",FACE,{"disambiguationData":[TD([[makeQuery(id+"F0.imprint","IMPRINT",EDGE,{"disambiguationData":[TD([[subQ2,-1.0]])],"derivedFrom":subQ1}),1.0]])]});}
            var Q41;
            {var subQ0=sQuery(id+"F0.wireOp",EDGE,"E16");var subQ1=sQuery(id+"F0.wireOp",EDGE,"E3");var subQ2=makeQuery(id+"F0.imprint","INTERSECT",VERTEX,{"derivedFrom":[subQ1,subQ0]});Q41=makeQuery(id+"F0.imprint","IMPRINT",FACE,{"disambiguationData":[TD([[makeQuery(id+"F0.imprint","IMPRINT",EDGE,{"disambiguationData":[TD([[subQ2,-1.0]])],"derivedFrom":subQ1}),1.0]])]});}
            var Q42;
            {var subQ0=sQuery(id+"F0.wireOp",EDGE,"E46");var subQ1=sQuery(id+"F0.wireOp",EDGE,"E3");var subQ2=makeQuery(id+"F0.imprint","INTERSECT",VERTEX,{"derivedFrom":[subQ1,subQ0]});Q42=makeQuery(id+"F0.imprint","IMPRINT",FACE,{"disambiguationData":[TD([[makeQuery(id+"F0.imprint","IMPRINT",EDGE,{"disambiguationData":[TD([[subQ2,-1.0]])],"derivedFrom":subQ1}),1.0]])]});}
            var Q43;
            {var subQ0=sQuery(id+"F0.wireOp",EDGE,"E21.11.0");var subQ1=sQuery(id+"F0.wireOp",EDGE,"E3");var subQ2=makeQuery(id+"F0.imprint","INTERSECT",VERTEX,{"derivedFrom":[subQ1,subQ0]});Q43=makeQuery(id+"F0.imprint","IMPRINT",FACE,{"disambiguationData":[TD([[makeQuery(id+"F0.imprint","IMPRINT",EDGE,{"disambiguationData":[TD([[subQ2,-1.0]])],"derivedFrom":subQ1}),-1.0]])]});}
            var Q44;
            {var subQ0=sQuery(id+"F0.wireOp",EDGE,"E47.11.0");var subQ1=sQuery(id+"F0.wireOp",EDGE,"E3");var subQ2=makeQuery(id+"F0.imprint","INTERSECT",VERTEX,{"derivedFrom":[subQ1,subQ0]});Q44=makeQuery(id+"F0.imprint","IMPRINT",FACE,{"disambiguationData":[TD([[makeQuery(id+"F0.imprint","IMPRINT",EDGE,{"disambiguationData":[TD([[subQ2,-1.0]])],"derivedFrom":subQ1}),-1.0]])]});}
            var Q45;
            {var subQ0=sQuery(id+"F0.wireOp",EDGE,"E47.11.1");var subQ1=sQuery(id+"F0.wireOp",EDGE,"E3");var subQ2=makeQuery(id+"F0.imprint","INTERSECT",VERTEX,{"derivedFrom":[subQ1,subQ0]});Q45=makeQuery(id+"F0.imprint","IMPRINT",FACE,{"disambiguationData":[TD([[makeQuery(id+"F0.imprint","IMPRINT",EDGE,{"disambiguationData":[TD([[subQ2,-1.0]])],"derivedFrom":subQ1}),1.0]])]});}
            var Q46;
            {var subQ0=sQuery(id+"F0.wireOp",EDGE,"E21.11.5");var subQ1=sQuery(id+"F0.wireOp",EDGE,"E3");var subQ2=makeQuery(id+"F0.imprint","INTERSECT",VERTEX,{"derivedFrom":[subQ1,subQ0]});Q46=makeQuery(id+"F0.imprint","IMPRINT",FACE,{"disambiguationData":[TD([[makeQuery(id+"F0.imprint","IMPRINT",EDGE,{"disambiguationData":[TD([[subQ2,-1.0]])],"derivedFrom":subQ1}),1.0]])]});}
            var Q47;
            {var subQ0=sQuery(id+"F0.wireOp",EDGE,"E47.11.0");var subQ1=sQuery(id+"F0.wireOp",EDGE,"E3");var subQ2=makeQuery(id+"F0.imprint","INTERSECT",VERTEX,{"derivedFrom":[subQ1,subQ0]});Q47=makeQuery(id+"F0.imprint","IMPRINT",FACE,{"disambiguationData":[TD([[makeQuery(id+"F0.imprint","IMPRINT",EDGE,{"disambiguationData":[TD([[subQ2,-1.0]])],"derivedFrom":subQ1}),1.0]])]});}
            var Q48;
            {var subQ0=sQuery(id+"F0.wireOp",EDGE,"E21.11.0");var subQ1=sQuery(id+"F0.wireOp",EDGE,"E3");var subQ2=makeQuery(id+"F0.imprint","INTERSECT",VERTEX,{"derivedFrom":[subQ1,subQ0]});Q48=makeQuery(id+"F0.imprint","IMPRINT",FACE,{"disambiguationData":[TD([[makeQuery(id+"F0.imprint","IMPRINT",EDGE,{"disambiguationData":[TD([[subQ2,-1.0]])],"derivedFrom":subQ1}),1.0]])]});}
            var Q49;
            {var subQ0=sQuery(id+"F0.wireOp",EDGE,"E21.10.0");var subQ1=sQuery(id+"F0.wireOp",EDGE,"E3");var subQ2=makeQuery(id+"F0.imprint","INTERSECT",VERTEX,{"derivedFrom":[subQ1,subQ0]});Q49=makeQuery(id+"F0.imprint","IMPRINT",FACE,{"disambiguationData":[TD([[makeQuery(id+"F0.imprint","IMPRINT",EDGE,{"disambiguationData":[TD([[subQ2,-1.0]])],"derivedFrom":subQ1}),-1.0]])]});}
            var Q50;
            {var subQ0=sQuery(id+"F0.wireOp",EDGE,"E21.10.0");var subQ1=sQuery(id+"F0.wireOp",EDGE,"E3");var subQ2=makeQuery(id+"F0.imprint","INTERSECT",VERTEX,{"derivedFrom":[subQ1,subQ0]});Q50=makeQuery(id+"F0.imprint","IMPRINT",FACE,{"disambiguationData":[TD([[makeQuery(id+"F0.imprint","IMPRINT",EDGE,{"disambiguationData":[TD([[subQ2,-1.0]])],"derivedFrom":subQ1}),1.0]])]});}
            var Q51;
            {var subQ0=sQuery(id+"F0.wireOp",EDGE,"E47.10.0");var subQ1=sQuery(id+"F0.wireOp",EDGE,"E3");var subQ2=makeQuery(id+"F0.imprint","INTERSECT",VERTEX,{"derivedFrom":[subQ1,subQ0]});Q51=makeQuery(id+"F0.imprint","IMPRINT",FACE,{"disambiguationData":[TD([[makeQuery(id+"F0.imprint","IMPRINT",EDGE,{"disambiguationData":[TD([[subQ2,-1.0]])],"derivedFrom":subQ1}),1.0]])]});}
            var Q52;
            {var subQ0=sQuery(id+"F0.wireOp",EDGE,"E47.10.0");var subQ1=sQuery(id+"F0.wireOp",EDGE,"E3");var subQ2=makeQuery(id+"F0.imprint","INTERSECT",VERTEX,{"derivedFrom":[subQ1,subQ0]});Q52=makeQuery(id+"F0.imprint","IMPRINT",FACE,{"disambiguationData":[TD([[makeQuery(id+"F0.imprint","IMPRINT",EDGE,{"disambiguationData":[TD([[subQ2,-1.0]])],"derivedFrom":subQ1}),-1.0]])]});}
            var Q53;
            {var subQ0=sQuery(id+"F0.wireOp",EDGE,"E47.1.0");var subQ1=sQuery(id+"F0.wireOp",EDGE,"E3");var subQ2=makeQuery(id+"F0.imprint","INTERSECT",VERTEX,{"derivedFrom":[subQ1,subQ0]});Q53=makeQuery(id+"F0.imprint","IMPRINT",FACE,{"disambiguationData":[TD([[makeQuery(id+"F0.imprint","IMPRINT",EDGE,{"disambiguationData":[TD([[subQ2,-1.0]])],"derivedFrom":subQ1}),-1.0]])]});}
            var Q54;
            {var subQ0=sQuery(id+"F0.wireOp",EDGE,"E21.1.0");var subQ1=sQuery(id+"F0.wireOp",EDGE,"E3");var subQ2=makeQuery(id+"F0.imprint","INTERSECT",VERTEX,{"derivedFrom":[subQ1,subQ0]});Q54=makeQuery(id+"F0.imprint","IMPRINT",FACE,{"disambiguationData":[TD([[makeQuery(id+"F0.imprint","IMPRINT",EDGE,{"disambiguationData":[TD([[subQ2,-1.0]])],"derivedFrom":subQ1}),-1.0]])]});}
            var Q55;
            {var subQ0=sQuery(id+"F0.wireOp",EDGE,"E21.1.0");var subQ1=sQuery(id+"F0.wireOp",EDGE,"E3");var subQ2=makeQuery(id+"F0.imprint","INTERSECT",VERTEX,{"derivedFrom":[subQ1,subQ0]});Q55=makeQuery(id+"F0.imprint","IMPRINT",FACE,{"disambiguationData":[TD([[makeQuery(id+"F0.imprint","IMPRINT",EDGE,{"disambiguationData":[TD([[subQ2,-1.0]])],"derivedFrom":subQ1}),1.0]])]});}
            var Q56;
            {var subQ0=sQuery(id+"F0.wireOp",EDGE,"E47.1.1");var subQ1=sQuery(id+"F0.wireOp",EDGE,"E3");var subQ2=makeQuery(id+"F0.imprint","INTERSECT",VERTEX,{"derivedFrom":[subQ1,subQ0]});Q56=makeQuery(id+"F0.imprint","IMPRINT",FACE,{"disambiguationData":[TD([[makeQuery(id+"F0.imprint","IMPRINT",EDGE,{"disambiguationData":[TD([[subQ2,-1.0]])],"derivedFrom":subQ1}),1.0]])]});}
            var Q57;
            {var subQ0=sQuery(id+"F0.wireOp",EDGE,"E47.1.0");var subQ1=sQuery(id+"F0.wireOp",EDGE,"E3");var subQ2=makeQuery(id+"F0.imprint","INTERSECT",VERTEX,{"derivedFrom":[subQ1,subQ0]});Q57=makeQuery(id+"F0.imprint","IMPRINT",FACE,{"disambiguationData":[TD([[makeQuery(id+"F0.imprint","IMPRINT",EDGE,{"disambiguationData":[TD([[subQ2,-1.0]])],"derivedFrom":subQ1}),1.0]])]});}
            var Q58;
            {var subQ0=sQuery(id+"F0.wireOp",EDGE,"E21.1.5");var subQ1=sQuery(id+"F0.wireOp",EDGE,"E3");var subQ2=makeQuery(id+"F0.imprint","INTERSECT",VERTEX,{"derivedFrom":[subQ1,subQ0]});Q58=makeQuery(id+"F0.imprint","IMPRINT",FACE,{"disambiguationData":[TD([[makeQuery(id+"F0.imprint","IMPRINT",EDGE,{"disambiguationData":[TD([[subQ2,-1.0]])],"derivedFrom":subQ1}),1.0]])]});}
            var Q59;
            {var subQ0=sQuery(id+"F0.wireOp",EDGE,"E21.2.5");var subQ1=sQuery(id+"F0.wireOp",EDGE,"E3");var subQ2=makeQuery(id+"F0.imprint","INTERSECT",VERTEX,{"derivedFrom":[subQ1,subQ0]});Q59=makeQuery(id+"F0.imprint","IMPRINT",FACE,{"disambiguationData":[TD([[makeQuery(id+"F0.imprint","IMPRINT",EDGE,{"disambiguationData":[TD([[subQ2,-1.0]])],"derivedFrom":subQ1}),1.0]])]});}
            var Q60;
            {var subQ0=sQuery(id+"F0.wireOp",EDGE,"E47.2.0");var subQ1=sQuery(id+"F0.wireOp",EDGE,"E3");var subQ2=makeQuery(id+"F0.imprint","INTERSECT",VERTEX,{"derivedFrom":[subQ1,subQ0]});Q60=makeQuery(id+"F0.imprint","IMPRINT",FACE,{"disambiguationData":[TD([[makeQuery(id+"F0.imprint","IMPRINT",EDGE,{"disambiguationData":[TD([[subQ2,-1.0]])],"derivedFrom":subQ1}),1.0]])]});}
            var Q61;
            {var subQ0=sQuery(id+"F0.wireOp",EDGE,"E21.2.0");var subQ1=sQuery(id+"F0.wireOp",EDGE,"E3");var subQ2=makeQuery(id+"F0.imprint","INTERSECT",VERTEX,{"derivedFrom":[subQ1,subQ0]});Q61=makeQuery(id+"F0.imprint","IMPRINT",FACE,{"disambiguationData":[TD([[makeQuery(id+"F0.imprint","IMPRINT",EDGE,{"disambiguationData":[TD([[subQ2,-1.0]])],"derivedFrom":subQ1}),1.0]])]});}
            var Q62;
            {var subQ0=sQuery(id+"F0.wireOp",EDGE,"E21.2.6");var subQ1=sQuery(id+"F0.wireOp",EDGE,"E3");var subQ2=makeQuery(id+"F0.imprint","INTERSECT",VERTEX,{"derivedFrom":[subQ1,subQ0]});Q62=makeQuery(id+"F0.imprint","IMPRINT",FACE,{"disambiguationData":[TD([[makeQuery(id+"F0.imprint","IMPRINT",EDGE,{"disambiguationData":[TD([[subQ2,1.0]])],"derivedFrom":subQ1}),1.0]])]});}
            var Q63;
            {var subQ0=sQuery(id+"F0.wireOp",EDGE,"E21.2.0");var subQ1=sQuery(id+"F0.wireOp",EDGE,"E3");var subQ2=makeQuery(id+"F0.imprint","INTERSECT",VERTEX,{"derivedFrom":[subQ1,subQ0]});Q63=makeQuery(id+"F0.imprint","IMPRINT",FACE,{"disambiguationData":[TD([[makeQuery(id+"F0.imprint","IMPRINT",EDGE,{"disambiguationData":[TD([[subQ2,-1.0]])],"derivedFrom":subQ1}),-1.0]])]});}
            var Q64;
            {var subQ0=sQuery(id+"F0.wireOp",EDGE,"E47.2.0");var subQ1=sQuery(id+"F0.wireOp",EDGE,"E3");var subQ2=makeQuery(id+"F0.imprint","INTERSECT",VERTEX,{"derivedFrom":[subQ1,subQ0]});Q64=makeQuery(id+"F0.imprint","IMPRINT",FACE,{"disambiguationData":[TD([[makeQuery(id+"F0.imprint","IMPRINT",EDGE,{"disambiguationData":[TD([[subQ2,-1.0]])],"derivedFrom":subQ1}),-1.0]])]});}
            var Q65;
            {var subQ0=sQuery(id+"F0.wireOp",EDGE,"E21.3.0");var subQ1=sQuery(id+"F0.wireOp",EDGE,"E3");var subQ2=makeQuery(id+"F0.imprint","INTERSECT",VERTEX,{"derivedFrom":[subQ1,subQ0]});Q65=makeQuery(id+"F0.imprint","IMPRINT",FACE,{"disambiguationData":[TD([[makeQuery(id+"F0.imprint","IMPRINT",EDGE,{"disambiguationData":[TD([[subQ2,-1.0]])],"derivedFrom":subQ1}),-1.0]])]});}
            var Q66;
            {var subQ0=sQuery(id+"F0.wireOp",EDGE,"E47.3.0");var subQ1=sQuery(id+"F0.wireOp",EDGE,"E3");var subQ2=makeQuery(id+"F0.imprint","INTERSECT",VERTEX,{"derivedFrom":[subQ1,subQ0]});Q66=makeQuery(id+"F0.imprint","IMPRINT",FACE,{"disambiguationData":[TD([[makeQuery(id+"F0.imprint","IMPRINT",EDGE,{"disambiguationData":[TD([[subQ2,-1.0]])],"derivedFrom":subQ1}),-1.0]])]});}
            var Q67;
            {var subQ0=sQuery(id+"F0.wireOp",EDGE,"E21.3.0");var subQ1=sQuery(id+"F0.wireOp",EDGE,"E3");var subQ2=makeQuery(id+"F0.imprint","INTERSECT",VERTEX,{"derivedFrom":[subQ1,subQ0]});Q67=makeQuery(id+"F0.imprint","IMPRINT",FACE,{"disambiguationData":[TD([[makeQuery(id+"F0.imprint","IMPRINT",EDGE,{"disambiguationData":[TD([[subQ2,-1.0]])],"derivedFrom":subQ1}),1.0]])]});}
            var Q68;
            {var subQ0=sQuery(id+"F0.wireOp",EDGE,"E47.3.1");var subQ1=sQuery(id+"F0.wireOp",EDGE,"E3");var subQ2=makeQuery(id+"F0.imprint","INTERSECT",VERTEX,{"derivedFrom":[subQ1,subQ0]});Q68=makeQuery(id+"F0.imprint","IMPRINT",FACE,{"disambiguationData":[TD([[makeQuery(id+"F0.imprint","IMPRINT",EDGE,{"disambiguationData":[TD([[subQ2,-1.0]])],"derivedFrom":subQ1}),1.0]])]});}
            var Q69;
            {var subQ0=sQuery(id+"F0.wireOp",EDGE,"E47.3.0");var subQ1=sQuery(id+"F0.wireOp",EDGE,"E3");var subQ2=makeQuery(id+"F0.imprint","INTERSECT",VERTEX,{"derivedFrom":[subQ1,subQ0]});Q69=makeQuery(id+"F0.imprint","IMPRINT",FACE,{"disambiguationData":[TD([[makeQuery(id+"F0.imprint","IMPRINT",EDGE,{"disambiguationData":[TD([[subQ2,-1.0]])],"derivedFrom":subQ1}),1.0]])]});}
            var Q70;
            {var subQ0=sQuery(id+"F0.wireOp",EDGE,"E21.3.5");var subQ1=sQuery(id+"F0.wireOp",EDGE,"E3");var subQ2=makeQuery(id+"F0.imprint","INTERSECT",VERTEX,{"derivedFrom":[subQ1,subQ0]});Q70=makeQuery(id+"F0.imprint","IMPRINT",FACE,{"disambiguationData":[TD([[makeQuery(id+"F0.imprint","IMPRINT",EDGE,{"disambiguationData":[TD([[subQ2,-1.0]])],"derivedFrom":subQ1}),1.0]])]});}
            var Q71;
            {var subQ0=sQuery(id+"F0.wireOp",EDGE,"E21.9.0");var subQ1=sQuery(id+"F0.wireOp",EDGE,"E3");var subQ2=makeQuery(id+"F0.imprint","INTERSECT",VERTEX,{"derivedFrom":[subQ1,subQ0]});Q71=makeQuery(id+"F0.imprint","IMPRINT",FACE,{"disambiguationData":[TD([[makeQuery(id+"F0.imprint","IMPRINT",EDGE,{"disambiguationData":[TD([[subQ2,-1.0]])],"derivedFrom":subQ1}),-1.0]])]});}
            var Q72;
            {var subQ0=sQuery(id+"F0.wireOp",EDGE,"E21.9.0");var subQ1=sQuery(id+"F0.wireOp",EDGE,"E3");var subQ2=makeQuery(id+"F0.imprint","INTERSECT",VERTEX,{"derivedFrom":[subQ1,subQ0]});Q72=makeQuery(id+"F0.imprint","IMPRINT",FACE,{"disambiguationData":[TD([[makeQuery(id+"F0.imprint","IMPRINT",EDGE,{"disambiguationData":[TD([[subQ2,-1.0]])],"derivedFrom":subQ1}),1.0]])]});}
            var Q73;
            {var subQ0=sQuery(id+"F0.wireOp",EDGE,"E47.9.1");var subQ1=sQuery(id+"F0.wireOp",EDGE,"E3");var subQ2=makeQuery(id+"F0.imprint","INTERSECT",VERTEX,{"derivedFrom":[subQ1,subQ0]});Q73=makeQuery(id+"F0.imprint","IMPRINT",FACE,{"disambiguationData":[TD([[makeQuery(id+"F0.imprint","IMPRINT",EDGE,{"disambiguationData":[TD([[subQ2,-1.0]])],"derivedFrom":subQ1}),1.0]])]});}
            var Q74;
            {var subQ0=sQuery(id+"F0.wireOp",EDGE,"E47.9.0");var subQ1=sQuery(id+"F0.wireOp",EDGE,"E3");var subQ2=makeQuery(id+"F0.imprint","INTERSECT",VERTEX,{"derivedFrom":[subQ1,subQ0]});Q74=makeQuery(id+"F0.imprint","IMPRINT",FACE,{"disambiguationData":[TD([[makeQuery(id+"F0.imprint","IMPRINT",EDGE,{"disambiguationData":[TD([[subQ2,-1.0]])],"derivedFrom":subQ1}),1.0]])]});}
            var Q75;
            {var subQ0=sQuery(id+"F0.wireOp",EDGE,"E47.9.0");var subQ1=sQuery(id+"F0.wireOp",EDGE,"E3");var subQ2=makeQuery(id+"F0.imprint","INTERSECT",VERTEX,{"derivedFrom":[subQ1,subQ0]});Q75=makeQuery(id+"F0.imprint","IMPRINT",FACE,{"disambiguationData":[TD([[makeQuery(id+"F0.imprint","IMPRINT",EDGE,{"disambiguationData":[TD([[subQ2,-1.0]])],"derivedFrom":subQ1}),-1.0]])]});}
            var Q76;
            {var subQ0=sQuery(id+"F0.wireOp",EDGE,"E21.9.5");var subQ1=sQuery(id+"F0.wireOp",EDGE,"E3");var subQ2=makeQuery(id+"F0.imprint","INTERSECT",VERTEX,{"derivedFrom":[subQ1,subQ0]});Q76=makeQuery(id+"F0.imprint","IMPRINT",FACE,{"disambiguationData":[TD([[makeQuery(id+"F0.imprint","IMPRINT",EDGE,{"disambiguationData":[TD([[subQ2,-1.0]])],"derivedFrom":subQ1}),1.0]])]});}
            var Q77;
            {var subQ0=sQuery(id+"F0.wireOp",EDGE,"E21.8.0");var subQ1=sQuery(id+"F0.wireOp",EDGE,"E3");var subQ2=makeQuery(id+"F0.imprint","INTERSECT",VERTEX,{"derivedFrom":[subQ1,subQ0]});Q77=makeQuery(id+"F0.imprint","IMPRINT",FACE,{"disambiguationData":[TD([[makeQuery(id+"F0.imprint","IMPRINT",EDGE,{"disambiguationData":[TD([[subQ2,-1.0]])],"derivedFrom":subQ1}),-1.0]])]});}
            var Q78;
            {var subQ0=sQuery(id+"F0.wireOp",EDGE,"E47.8.0");var subQ1=sQuery(id+"F0.wireOp",EDGE,"E3");var subQ2=makeQuery(id+"F0.imprint","INTERSECT",VERTEX,{"derivedFrom":[subQ1,subQ0]});Q78=makeQuery(id+"F0.imprint","IMPRINT",FACE,{"disambiguationData":[TD([[makeQuery(id+"F0.imprint","IMPRINT",EDGE,{"disambiguationData":[TD([[subQ2,-1.0]])],"derivedFrom":subQ1}),-1.0]])]});}
            var Q79;
            {var subQ0=sQuery(id+"F0.wireOp",EDGE,"E21.8.0");var subQ1=sQuery(id+"F0.wireOp",EDGE,"E3");var subQ2=makeQuery(id+"F0.imprint","INTERSECT",VERTEX,{"derivedFrom":[subQ1,subQ0]});Q79=makeQuery(id+"F0.imprint","IMPRINT",FACE,{"disambiguationData":[TD([[makeQuery(id+"F0.imprint","IMPRINT",EDGE,{"disambiguationData":[TD([[subQ2,-1.0]])],"derivedFrom":subQ1}),1.0]])]});}
            var Q80;
            {var subQ0=sQuery(id+"F0.wireOp",EDGE,"E47.8.0");var subQ1=sQuery(id+"F0.wireOp",EDGE,"E3");var subQ2=makeQuery(id+"F0.imprint","INTERSECT",VERTEX,{"derivedFrom":[subQ1,subQ0]});Q80=makeQuery(id+"F0.imprint","IMPRINT",FACE,{"disambiguationData":[TD([[makeQuery(id+"F0.imprint","IMPRINT",EDGE,{"disambiguationData":[TD([[subQ2,-1.0]])],"derivedFrom":subQ1}),1.0]])]});}
            var Q81;
            {var subQ0=sQuery(id+"F0.wireOp",EDGE,"E21.7.0");var subQ1=sQuery(id+"F0.wireOp",EDGE,"E3");var subQ2=makeQuery(id+"F0.imprint","INTERSECT",VERTEX,{"derivedFrom":[subQ1,subQ0]});Q81=makeQuery(id+"F0.imprint","IMPRINT",FACE,{"disambiguationData":[TD([[makeQuery(id+"F0.imprint","IMPRINT",EDGE,{"disambiguationData":[TD([[subQ2,-1.0]])],"derivedFrom":subQ1}),-1.0]])]});}
            var Q82;
            {var subQ0=sQuery(id+"F0.wireOp",EDGE,"E47.7.0");var subQ1=sQuery(id+"F0.wireOp",EDGE,"E3");var subQ2=makeQuery(id+"F0.imprint","INTERSECT",VERTEX,{"derivedFrom":[subQ1,subQ0]});Q82=makeQuery(id+"F0.imprint","IMPRINT",FACE,{"disambiguationData":[TD([[makeQuery(id+"F0.imprint","IMPRINT",EDGE,{"disambiguationData":[TD([[subQ2,-1.0]])],"derivedFrom":subQ1}),-1.0]])]});}
            var Q83;
            {var subQ0=sQuery(id+"F0.wireOp",EDGE,"E47.7.0");var subQ1=sQuery(id+"F0.wireOp",EDGE,"E3");var subQ2=makeQuery(id+"F0.imprint","INTERSECT",VERTEX,{"derivedFrom":[subQ1,subQ0]});Q83=makeQuery(id+"F0.imprint","IMPRINT",FACE,{"disambiguationData":[TD([[makeQuery(id+"F0.imprint","IMPRINT",EDGE,{"disambiguationData":[TD([[subQ2,-1.0]])],"derivedFrom":subQ1}),1.0]])]});}
            var Q84;
            {var subQ0=sQuery(id+"F0.wireOp",EDGE,"E21.7.0");var subQ1=sQuery(id+"F0.wireOp",EDGE,"E3");var subQ2=makeQuery(id+"F0.imprint","INTERSECT",VERTEX,{"derivedFrom":[subQ1,subQ0]});Q84=makeQuery(id+"F0.imprint","IMPRINT",FACE,{"disambiguationData":[TD([[makeQuery(id+"F0.imprint","IMPRINT",EDGE,{"disambiguationData":[TD([[subQ2,-1.0]])],"derivedFrom":subQ1}),1.0]])]});}
            var Q85;
            {var subQ0=sQuery(id+"F0.wireOp",EDGE,"E21.8.5");var subQ1=sQuery(id+"F0.wireOp",EDGE,"E3");var subQ2=makeQuery(id+"F0.imprint","INTERSECT",VERTEX,{"derivedFrom":[subQ1,subQ0]});Q85=makeQuery(id+"F0.imprint","IMPRINT",FACE,{"disambiguationData":[TD([[makeQuery(id+"F0.imprint","IMPRINT",EDGE,{"disambiguationData":[TD([[subQ2,-1.0]])],"derivedFrom":subQ1}),1.0]])]});}
            var Q86;
            {var subQ0=sQuery(id+"F0.wireOp",EDGE,"E47.8.1");var subQ1=sQuery(id+"F0.wireOp",EDGE,"E3");var subQ2=makeQuery(id+"F0.imprint","INTERSECT",VERTEX,{"derivedFrom":[subQ1,subQ0]});Q86=makeQuery(id+"F0.imprint","IMPRINT",FACE,{"disambiguationData":[TD([[makeQuery(id+"F0.imprint","IMPRINT",EDGE,{"disambiguationData":[TD([[subQ2,-1.0]])],"derivedFrom":subQ1}),1.0]])]});}
            var Q87;
            {var subQ0=sQuery(id+"F0.wireOp",EDGE,"E21.10.5");var subQ1=sQuery(id+"F0.wireOp",EDGE,"E3");var subQ2=makeQuery(id+"F0.imprint","INTERSECT",VERTEX,{"derivedFrom":[subQ1,subQ0]});Q87=makeQuery(id+"F0.imprint","IMPRINT",FACE,{"disambiguationData":[TD([[makeQuery(id+"F0.imprint","IMPRINT",EDGE,{"disambiguationData":[TD([[subQ2,-1.0]])],"derivedFrom":subQ1}),1.0]])]});}
            var Q88;
            {var subQ0=sQuery(id+"F0.wireOp",EDGE,"E47.10.1");var subQ1=sQuery(id+"F0.wireOp",EDGE,"E3");var subQ2=makeQuery(id+"F0.imprint","INTERSECT",VERTEX,{"derivedFrom":[subQ1,subQ0]});Q88=makeQuery(id+"F0.imprint","IMPRINT",FACE,{"disambiguationData":[TD([[makeQuery(id+"F0.imprint","IMPRINT",EDGE,{"disambiguationData":[TD([[subQ2,-1.0]])],"derivedFrom":subQ1}),1.0]])]});}
            var Q89;
            {var subQ0=sQuery(id+"F0.wireOp",EDGE,"E21.6.0");var subQ1=sQuery(id+"F0.wireOp",EDGE,"E3");var subQ2=makeQuery(id+"F0.imprint","INTERSECT",VERTEX,{"derivedFrom":[subQ1,subQ0]});Q89=makeQuery(id+"F0.imprint","IMPRINT",FACE,{"disambiguationData":[TD([[makeQuery(id+"F0.imprint","IMPRINT",EDGE,{"disambiguationData":[TD([[subQ2,-1.0]])],"derivedFrom":subQ1}),-1.0]])]});}
            var Q90;
            {var subQ0=sQuery(id+"F0.wireOp",EDGE,"E47.6.0");var subQ1=sQuery(id+"F0.wireOp",EDGE,"E3");var subQ2=makeQuery(id+"F0.imprint","INTERSECT",VERTEX,{"derivedFrom":[subQ1,subQ0]});Q90=makeQuery(id+"F0.imprint","IMPRINT",FACE,{"disambiguationData":[TD([[makeQuery(id+"F0.imprint","IMPRINT",EDGE,{"disambiguationData":[TD([[subQ2,-1.0]])],"derivedFrom":subQ1}),-1.0]])]});}
            var Q91;
            {var subQ0=sQuery(id+"F0.wireOp",EDGE,"E47.6.0");var subQ1=sQuery(id+"F0.wireOp",EDGE,"E3");var subQ2=makeQuery(id+"F0.imprint","INTERSECT",VERTEX,{"derivedFrom":[subQ1,subQ0]});Q91=makeQuery(id+"F0.imprint","IMPRINT",FACE,{"disambiguationData":[TD([[makeQuery(id+"F0.imprint","IMPRINT",EDGE,{"disambiguationData":[TD([[subQ2,-1.0]])],"derivedFrom":subQ1}),1.0]])]});}
            var Q92;
            {var subQ0=sQuery(id+"F0.wireOp",EDGE,"E21.6.5");var subQ1=sQuery(id+"F0.wireOp",EDGE,"E3");var subQ2=makeQuery(id+"F0.imprint","INTERSECT",VERTEX,{"derivedFrom":[subQ1,subQ0]});Q92=makeQuery(id+"F0.imprint","IMPRINT",FACE,{"disambiguationData":[TD([[makeQuery(id+"F0.imprint","IMPRINT",EDGE,{"disambiguationData":[TD([[subQ2,-1.0]])],"derivedFrom":subQ1}),1.0]])]});}
            var Q93;
            {var subQ0=sQuery(id+"F0.wireOp",EDGE,"E47.6.1");var subQ1=sQuery(id+"F0.wireOp",EDGE,"E3");var subQ2=makeQuery(id+"F0.imprint","INTERSECT",VERTEX,{"derivedFrom":[subQ1,subQ0]});Q93=makeQuery(id+"F0.imprint","IMPRINT",FACE,{"disambiguationData":[TD([[makeQuery(id+"F0.imprint","IMPRINT",EDGE,{"disambiguationData":[TD([[subQ2,-1.0]])],"derivedFrom":subQ1}),1.0]])]});}
            var Q94;
            {var subQ0=sQuery(id+"F0.wireOp",EDGE,"E21.7.5");var subQ1=sQuery(id+"F0.wireOp",EDGE,"E3");var subQ2=makeQuery(id+"F0.imprint","INTERSECT",VERTEX,{"derivedFrom":[subQ1,subQ0]});Q94=makeQuery(id+"F0.imprint","IMPRINT",FACE,{"disambiguationData":[TD([[makeQuery(id+"F0.imprint","IMPRINT",EDGE,{"disambiguationData":[TD([[subQ2,-1.0]])],"derivedFrom":subQ1}),1.0]])]});}
            var Q95;
            {var subQ0=sQuery(id+"F0.wireOp",EDGE,"E47.7.1");var subQ1=sQuery(id+"F0.wireOp",EDGE,"E3");var subQ2=makeQuery(id+"F0.imprint","INTERSECT",VERTEX,{"derivedFrom":[subQ1,subQ0]});Q95=makeQuery(id+"F0.imprint","IMPRINT",FACE,{"disambiguationData":[TD([[makeQuery(id+"F0.imprint","IMPRINT",EDGE,{"disambiguationData":[TD([[subQ2,-1.0]])],"derivedFrom":subQ1}),1.0]])]});}
            var Q96;
            {var subQ0=sQuery(id+"F0.wireOp",EDGE,"E47.5.1");var subQ1=sQuery(id+"F0.wireOp",EDGE,"E3");var subQ2=makeQuery(id+"F0.imprint","INTERSECT",VERTEX,{"derivedFrom":[subQ1,subQ0]});Q96=makeQuery(id+"F0.imprint","IMPRINT",FACE,{"disambiguationData":[TD([[makeQuery(id+"F0.imprint","IMPRINT",EDGE,{"disambiguationData":[TD([[subQ2,-1.0]])],"derivedFrom":subQ1}),1.0]])]});}
            var Q97;
            {var subQ0=sQuery(id+"F0.wireOp",EDGE,"E21.5.0");var subQ1=sQuery(id+"F0.wireOp",EDGE,"E3");var subQ2=makeQuery(id+"F0.imprint","INTERSECT",VERTEX,{"derivedFrom":[subQ1,subQ0]});Q97=makeQuery(id+"F0.imprint","IMPRINT",FACE,{"disambiguationData":[TD([[makeQuery(id+"F0.imprint","IMPRINT",EDGE,{"disambiguationData":[TD([[subQ2,-1.0]])],"derivedFrom":subQ1}),1.0]])]});}
            var Q98;
            {var subQ0=sQuery(id+"F0.wireOp",EDGE,"E47.5.0");var subQ1=sQuery(id+"F0.wireOp",EDGE,"E3");var subQ2=makeQuery(id+"F0.imprint","INTERSECT",VERTEX,{"derivedFrom":[subQ1,subQ0]});Q98=makeQuery(id+"F0.imprint","IMPRINT",FACE,{"disambiguationData":[TD([[makeQuery(id+"F0.imprint","IMPRINT",EDGE,{"disambiguationData":[TD([[subQ2,-1.0]])],"derivedFrom":subQ1}),1.0]])]});}
            var Q99;
            {var subQ0=sQuery(id+"F0.wireOp",EDGE,"E21.5.5");var subQ1=sQuery(id+"F0.wireOp",EDGE,"E3");var subQ2=makeQuery(id+"F0.imprint","INTERSECT",VERTEX,{"derivedFrom":[subQ1,subQ0]});Q99=makeQuery(id+"F0.imprint","IMPRINT",FACE,{"disambiguationData":[TD([[makeQuery(id+"F0.imprint","IMPRINT",EDGE,{"disambiguationData":[TD([[subQ2,-1.0]])],"derivedFrom":subQ1}),1.0]])]});}
            var Q100;
            {var subQ0=sQuery(id+"F0.wireOp",EDGE,"E21.6.0");var subQ1=sQuery(id+"F0.wireOp",EDGE,"E3");var subQ2=makeQuery(id+"F0.imprint","INTERSECT",VERTEX,{"derivedFrom":[subQ1,subQ0]});Q100=makeQuery(id+"F0.imprint","IMPRINT",FACE,{"disambiguationData":[TD([[makeQuery(id+"F0.imprint","IMPRINT",EDGE,{"disambiguationData":[TD([[subQ2,-1.0]])],"derivedFrom":subQ1}),1.0]])]});}
            var Q101;
            {var subQ0=sQuery(id+"F0.wireOp",EDGE,"E47.4.1");var subQ1=sQuery(id+"F0.wireOp",EDGE,"E3");var subQ2=makeQuery(id+"F0.imprint","INTERSECT",VERTEX,{"derivedFrom":[subQ1,subQ0]});Q101=makeQuery(id+"F0.imprint","IMPRINT",FACE,{"disambiguationData":[TD([[makeQuery(id+"F0.imprint","IMPRINT",EDGE,{"disambiguationData":[TD([[subQ2,-1.0]])],"derivedFrom":subQ1}),1.0]])]});}
            var Q102;
            {var subQ0=sQuery(id+"F0.wireOp",EDGE,"E21.4.0");var subQ1=sQuery(id+"F0.wireOp",EDGE,"E3");var subQ2=makeQuery(id+"F0.imprint","INTERSECT",VERTEX,{"derivedFrom":[subQ1,subQ0]});Q102=makeQuery(id+"F0.imprint","IMPRINT",FACE,{"disambiguationData":[TD([[makeQuery(id+"F0.imprint","IMPRINT",EDGE,{"disambiguationData":[TD([[subQ2,-1.0]])],"derivedFrom":subQ1}),1.0]])]});}
            var Q103;
            {var subQ0=sQuery(id+"F0.wireOp",EDGE,"E21.4.0");var subQ1=sQuery(id+"F0.wireOp",EDGE,"E3");var subQ2=makeQuery(id+"F0.imprint","INTERSECT",VERTEX,{"derivedFrom":[subQ1,subQ0]});Q103=makeQuery(id+"F0.imprint","IMPRINT",FACE,{"disambiguationData":[TD([[makeQuery(id+"F0.imprint","IMPRINT",EDGE,{"disambiguationData":[TD([[subQ2,-1.0]])],"derivedFrom":subQ1}),-1.0]])]});}
            var Q104;
            {var subQ0=sQuery(id+"F0.wireOp",EDGE,"E47.4.0");var subQ1=sQuery(id+"F0.wireOp",EDGE,"E3");var subQ2=makeQuery(id+"F0.imprint","INTERSECT",VERTEX,{"derivedFrom":[subQ1,subQ0]});Q104=makeQuery(id+"F0.imprint","IMPRINT",FACE,{"disambiguationData":[TD([[makeQuery(id+"F0.imprint","IMPRINT",EDGE,{"disambiguationData":[TD([[subQ2,-1.0]])],"derivedFrom":subQ1}),-1.0]])]});}
            var Q105;
            {var subQ0=sQuery(id+"F0.wireOp",EDGE,"E47.4.0");var subQ1=sQuery(id+"F0.wireOp",EDGE,"E3");var subQ2=makeQuery(id+"F0.imprint","INTERSECT",VERTEX,{"derivedFrom":[subQ1,subQ0]});Q105=makeQuery(id+"F0.imprint","IMPRINT",FACE,{"disambiguationData":[TD([[makeQuery(id+"F0.imprint","IMPRINT",EDGE,{"disambiguationData":[TD([[subQ2,-1.0]])],"derivedFrom":subQ1}),1.0]])]});}
            var Q106;
            {var subQ0=sQuery(id+"F0.wireOp",EDGE,"E21.4.5");var subQ1=sQuery(id+"F0.wireOp",EDGE,"E3");var subQ2=makeQuery(id+"F0.imprint","INTERSECT",VERTEX,{"derivedFrom":[subQ1,subQ0]});Q106=makeQuery(id+"F0.imprint","IMPRINT",FACE,{"disambiguationData":[TD([[makeQuery(id+"F0.imprint","IMPRINT",EDGE,{"disambiguationData":[TD([[subQ2,-1.0]])],"derivedFrom":subQ1}),1.0]])]});}
            var Q107;
            {var subQ0=sQuery(id+"F0.wireOp",EDGE,"E21.5.0");var subQ1=sQuery(id+"F0.wireOp",EDGE,"E3");var subQ2=makeQuery(id+"F0.imprint","INTERSECT",VERTEX,{"derivedFrom":[subQ1,subQ0]});Q107=makeQuery(id+"F0.imprint","IMPRINT",FACE,{"disambiguationData":[TD([[makeQuery(id+"F0.imprint","IMPRINT",EDGE,{"disambiguationData":[TD([[subQ2,-1.0]])],"derivedFrom":subQ1}),-1.0]])]});}
            var Q108;
            {var subQ0=sQuery(id+"F0.wireOp",EDGE,"E47.5.0");var subQ1=sQuery(id+"F0.wireOp",EDGE,"E3");var subQ2=makeQuery(id+"F0.imprint","INTERSECT",VERTEX,{"derivedFrom":[subQ1,subQ0]});Q108=makeQuery(id+"F0.imprint","IMPRINT",FACE,{"disambiguationData":[TD([[makeQuery(id+"F0.imprint","IMPRINT",EDGE,{"disambiguationData":[TD([[subQ2,-1.0]])],"derivedFrom":subQ1}),-1.0]])]});}
            extrude(context, id + "F1", {"entities" : qUnion([Q0, Q1, Q2, Q3, Q4, Q5, Q6, Q7, Q8, Q9, Q10, Q11, Q12, Q13, Q14, Q15, Q16, Q17, Q18, Q19, Q20, Q21, Q22, Q23, Q24, Q25, Q26, Q27, Q28, Q29, Q30, Q31, Q32, Q33, Q34, Q35, Q36, Q37, Q38, Q39, Q40, Q41, Q42, Q43, Q44, Q45, Q46, Q47, Q48, Q49, Q50, Q51, Q52, Q53, Q54, Q55, Q56, Q57, Q58, Q59, Q60, Q61, Q62, Q63, Q64, Q65, Q66, Q67, Q68, Q69, Q70, Q71, Q72, Q73, Q74, Q75, Q76, Q77, Q78, Q79, Q80, Q81, Q82, Q83, Q84, Q85, Q86, Q87, Q88, Q89, Q90, Q91, Q92, Q93, Q94, Q95, Q96, Q97, Q98, Q99, Q100, Q101, Q102, Q103, Q104, Q105, Q106, Q107, Q108]), "depth" : 5 * mm});
        }
        {
            var Q0;
            {var subQ3=sQuery(id+"F0.wireOp",EDGE,"E3");var subQ7=sQuery(id+"F0.wireOp",EDGE,"E45");var subQ9=makeQuery(id+"F0.imprint","INTERSECT",VERTEX,{"derivedFrom":[subQ3,subQ7]});Q0=makeQuery(id+"F0.imprint","IMPRINT",FACE,{"disambiguationData":[TD([[makeQuery(id+"F0.imprint","IMPRINT",EDGE,{"disambiguationData":[TD([[subQ9,-1.0]])],"derivedFrom":subQ3}),-1.0]])]});}
            var Q1;
            {var subQ0=sQuery(id+"F0.wireOp",EDGE,"E16");var subQ3=sQuery(id+"F0.wireOp",EDGE,"E3");var subQ4=makeQuery(id+"F0.imprint","INTERSECT",VERTEX,{"derivedFrom":[subQ3,subQ0]});Q1=makeQuery(id+"F0.imprint","IMPRINT",FACE,{"disambiguationData":[TD([[makeQuery(id+"F0.imprint","IMPRINT",EDGE,{"disambiguationData":[TD([[subQ4,-1.0]])],"derivedFrom":subQ3}),-1.0]])]});}
            var Q2;
            {var subQ0=sQuery(id+"F0.wireOp",EDGE,"E47.1.0");var subQ1=sQuery(id+"F0.wireOp",EDGE,"E3");var subQ2=makeQuery(id+"F0.imprint","INTERSECT",VERTEX,{"derivedFrom":[subQ1,subQ0]});Q2=makeQuery(id+"F0.imprint","IMPRINT",FACE,{"disambiguationData":[TD([[makeQuery(id+"F0.imprint","IMPRINT",EDGE,{"disambiguationData":[TD([[subQ2,-1.0]])],"derivedFrom":subQ1}),-1.0]])]});}
            var Q3;
            {var subQ0=sQuery(id+"F0.wireOp",EDGE,"E21.1.0");var subQ1=sQuery(id+"F0.wireOp",EDGE,"E3");var subQ2=makeQuery(id+"F0.imprint","INTERSECT",VERTEX,{"derivedFrom":[subQ1,subQ0]});Q3=makeQuery(id+"F0.imprint","IMPRINT",FACE,{"disambiguationData":[TD([[makeQuery(id+"F0.imprint","IMPRINT",EDGE,{"disambiguationData":[TD([[subQ2,-1.0]])],"derivedFrom":subQ1}),-1.0]])]});}
            var Q4;
            {var subQ0=sQuery(id+"F0.wireOp",EDGE,"E47.2.0");var subQ1=sQuery(id+"F0.wireOp",EDGE,"E3");var subQ2=makeQuery(id+"F0.imprint","INTERSECT",VERTEX,{"derivedFrom":[subQ1,subQ0]});Q4=makeQuery(id+"F0.imprint","IMPRINT",FACE,{"disambiguationData":[TD([[makeQuery(id+"F0.imprint","IMPRINT",EDGE,{"disambiguationData":[TD([[subQ2,-1.0]])],"derivedFrom":subQ1}),-1.0]])]});}
            var Q5;
            {var subQ0=sQuery(id+"F0.wireOp",EDGE,"E21.2.0");var subQ1=sQuery(id+"F0.wireOp",EDGE,"E3");var subQ2=makeQuery(id+"F0.imprint","INTERSECT",VERTEX,{"derivedFrom":[subQ1,subQ0]});Q5=makeQuery(id+"F0.imprint","IMPRINT",FACE,{"disambiguationData":[TD([[makeQuery(id+"F0.imprint","IMPRINT",EDGE,{"disambiguationData":[TD([[subQ2,-1.0]])],"derivedFrom":subQ1}),-1.0]])]});}
            var Q6;
            {var subQ0=sQuery(id+"F0.wireOp",EDGE,"E21.11.0");var subQ1=sQuery(id+"F0.wireOp",EDGE,"E3");var subQ2=makeQuery(id+"F0.imprint","INTERSECT",VERTEX,{"derivedFrom":[subQ1,subQ0]});Q6=makeQuery(id+"F0.imprint","IMPRINT",FACE,{"disambiguationData":[TD([[makeQuery(id+"F0.imprint","IMPRINT",EDGE,{"disambiguationData":[TD([[subQ2,-1.0]])],"derivedFrom":subQ1}),-1.0]])]});}
            var Q7;
            {var subQ0=sQuery(id+"F0.wireOp",EDGE,"E47.11.0");var subQ1=sQuery(id+"F0.wireOp",EDGE,"E3");var subQ2=makeQuery(id+"F0.imprint","INTERSECT",VERTEX,{"derivedFrom":[subQ1,subQ0]});Q7=makeQuery(id+"F0.imprint","IMPRINT",FACE,{"disambiguationData":[TD([[makeQuery(id+"F0.imprint","IMPRINT",EDGE,{"disambiguationData":[TD([[subQ2,-1.0]])],"derivedFrom":subQ1}),-1.0]])]});}
            var Q8;
            {var subQ0=sQuery(id+"F0.wireOp",EDGE,"E21.10.0");var subQ1=sQuery(id+"F0.wireOp",EDGE,"E3");var subQ2=makeQuery(id+"F0.imprint","INTERSECT",VERTEX,{"derivedFrom":[subQ1,subQ0]});Q8=makeQuery(id+"F0.imprint","IMPRINT",FACE,{"disambiguationData":[TD([[makeQuery(id+"F0.imprint","IMPRINT",EDGE,{"disambiguationData":[TD([[subQ2,-1.0]])],"derivedFrom":subQ1}),-1.0]])]});}
            var Q9;
            {var subQ0=sQuery(id+"F0.wireOp",EDGE,"E47.10.0");var subQ1=sQuery(id+"F0.wireOp",EDGE,"E3");var subQ2=makeQuery(id+"F0.imprint","INTERSECT",VERTEX,{"derivedFrom":[subQ1,subQ0]});Q9=makeQuery(id+"F0.imprint","IMPRINT",FACE,{"disambiguationData":[TD([[makeQuery(id+"F0.imprint","IMPRINT",EDGE,{"disambiguationData":[TD([[subQ2,-1.0]])],"derivedFrom":subQ1}),-1.0]])]});}
            var Q10;
            {var subQ0=sQuery(id+"F0.wireOp",EDGE,"E47.3.0");var subQ1=sQuery(id+"F0.wireOp",EDGE,"E3");var subQ2=makeQuery(id+"F0.imprint","INTERSECT",VERTEX,{"derivedFrom":[subQ1,subQ0]});Q10=makeQuery(id+"F0.imprint","IMPRINT",FACE,{"disambiguationData":[TD([[makeQuery(id+"F0.imprint","IMPRINT",EDGE,{"disambiguationData":[TD([[subQ2,-1.0]])],"derivedFrom":subQ1}),-1.0]])]});}
            var Q11;
            {var subQ0=sQuery(id+"F0.wireOp",EDGE,"E21.3.0");var subQ1=sQuery(id+"F0.wireOp",EDGE,"E3");var subQ2=makeQuery(id+"F0.imprint","INTERSECT",VERTEX,{"derivedFrom":[subQ1,subQ0]});Q11=makeQuery(id+"F0.imprint","IMPRINT",FACE,{"disambiguationData":[TD([[makeQuery(id+"F0.imprint","IMPRINT",EDGE,{"disambiguationData":[TD([[subQ2,-1.0]])],"derivedFrom":subQ1}),-1.0]])]});}
            var Q12;
            {var subQ0=sQuery(id+"F0.wireOp",EDGE,"E47.4.0");var subQ1=sQuery(id+"F0.wireOp",EDGE,"E3");var subQ2=makeQuery(id+"F0.imprint","INTERSECT",VERTEX,{"derivedFrom":[subQ1,subQ0]});Q12=makeQuery(id+"F0.imprint","IMPRINT",FACE,{"disambiguationData":[TD([[makeQuery(id+"F0.imprint","IMPRINT",EDGE,{"disambiguationData":[TD([[subQ2,-1.0]])],"derivedFrom":subQ1}),-1.0]])]});}
            var Q13;
            {var subQ0=sQuery(id+"F0.wireOp",EDGE,"E21.4.0");var subQ1=sQuery(id+"F0.wireOp",EDGE,"E3");var subQ2=makeQuery(id+"F0.imprint","INTERSECT",VERTEX,{"derivedFrom":[subQ1,subQ0]});Q13=makeQuery(id+"F0.imprint","IMPRINT",FACE,{"disambiguationData":[TD([[makeQuery(id+"F0.imprint","IMPRINT",EDGE,{"disambiguationData":[TD([[subQ2,-1.0]])],"derivedFrom":subQ1}),-1.0]])]});}
            var Q14;
            {var subQ0=sQuery(id+"F0.wireOp",EDGE,"E47.5.0");var subQ1=sQuery(id+"F0.wireOp",EDGE,"E3");var subQ2=makeQuery(id+"F0.imprint","INTERSECT",VERTEX,{"derivedFrom":[subQ1,subQ0]});Q14=makeQuery(id+"F0.imprint","IMPRINT",FACE,{"disambiguationData":[TD([[makeQuery(id+"F0.imprint","IMPRINT",EDGE,{"disambiguationData":[TD([[subQ2,-1.0]])],"derivedFrom":subQ1}),-1.0]])]});}
            var Q15;
            {var subQ0=sQuery(id+"F0.wireOp",EDGE,"E21.5.0");var subQ1=sQuery(id+"F0.wireOp",EDGE,"E3");var subQ2=makeQuery(id+"F0.imprint","INTERSECT",VERTEX,{"derivedFrom":[subQ1,subQ0]});Q15=makeQuery(id+"F0.imprint","IMPRINT",FACE,{"disambiguationData":[TD([[makeQuery(id+"F0.imprint","IMPRINT",EDGE,{"disambiguationData":[TD([[subQ2,-1.0]])],"derivedFrom":subQ1}),-1.0]])]});}
            var Q16;
            {var subQ0=sQuery(id+"F0.wireOp",EDGE,"E47.6.0");var subQ1=sQuery(id+"F0.wireOp",EDGE,"E3");var subQ2=makeQuery(id+"F0.imprint","INTERSECT",VERTEX,{"derivedFrom":[subQ1,subQ0]});Q16=makeQuery(id+"F0.imprint","IMPRINT",FACE,{"disambiguationData":[TD([[makeQuery(id+"F0.imprint","IMPRINT",EDGE,{"disambiguationData":[TD([[subQ2,-1.0]])],"derivedFrom":subQ1}),-1.0]])]});}
            var Q17;
            {var subQ0=sQuery(id+"F0.wireOp",EDGE,"E21.6.0");var subQ1=sQuery(id+"F0.wireOp",EDGE,"E3");var subQ2=makeQuery(id+"F0.imprint","INTERSECT",VERTEX,{"derivedFrom":[subQ1,subQ0]});Q17=makeQuery(id+"F0.imprint","IMPRINT",FACE,{"disambiguationData":[TD([[makeQuery(id+"F0.imprint","IMPRINT",EDGE,{"disambiguationData":[TD([[subQ2,-1.0]])],"derivedFrom":subQ1}),-1.0]])]});}
            var Q18;
            {var subQ0=sQuery(id+"F0.wireOp",EDGE,"E47.7.0");var subQ1=sQuery(id+"F0.wireOp",EDGE,"E3");var subQ2=makeQuery(id+"F0.imprint","INTERSECT",VERTEX,{"derivedFrom":[subQ1,subQ0]});Q18=makeQuery(id+"F0.imprint","IMPRINT",FACE,{"disambiguationData":[TD([[makeQuery(id+"F0.imprint","IMPRINT",EDGE,{"disambiguationData":[TD([[subQ2,-1.0]])],"derivedFrom":subQ1}),-1.0]])]});}
            var Q19;
            {var subQ0=sQuery(id+"F0.wireOp",EDGE,"E21.7.0");var subQ1=sQuery(id+"F0.wireOp",EDGE,"E3");var subQ2=makeQuery(id+"F0.imprint","INTERSECT",VERTEX,{"derivedFrom":[subQ1,subQ0]});Q19=makeQuery(id+"F0.imprint","IMPRINT",FACE,{"disambiguationData":[TD([[makeQuery(id+"F0.imprint","IMPRINT",EDGE,{"disambiguationData":[TD([[subQ2,-1.0]])],"derivedFrom":subQ1}),-1.0]])]});}
            var Q20;
            {var subQ0=sQuery(id+"F0.wireOp",EDGE,"E47.8.0");var subQ1=sQuery(id+"F0.wireOp",EDGE,"E3");var subQ2=makeQuery(id+"F0.imprint","INTERSECT",VERTEX,{"derivedFrom":[subQ1,subQ0]});Q20=makeQuery(id+"F0.imprint","IMPRINT",FACE,{"disambiguationData":[TD([[makeQuery(id+"F0.imprint","IMPRINT",EDGE,{"disambiguationData":[TD([[subQ2,-1.0]])],"derivedFrom":subQ1}),-1.0]])]});}
            var Q21;
            {var subQ0=sQuery(id+"F0.wireOp",EDGE,"E21.8.0");var subQ1=sQuery(id+"F0.wireOp",EDGE,"E3");var subQ2=makeQuery(id+"F0.imprint","INTERSECT",VERTEX,{"derivedFrom":[subQ1,subQ0]});Q21=makeQuery(id+"F0.imprint","IMPRINT",FACE,{"disambiguationData":[TD([[makeQuery(id+"F0.imprint","IMPRINT",EDGE,{"disambiguationData":[TD([[subQ2,-1.0]])],"derivedFrom":subQ1}),-1.0]])]});}
            var Q22;
            {var subQ0=sQuery(id+"F0.wireOp",EDGE,"E47.9.0");var subQ1=sQuery(id+"F0.wireOp",EDGE,"E3");var subQ2=makeQuery(id+"F0.imprint","INTERSECT",VERTEX,{"derivedFrom":[subQ1,subQ0]});Q22=makeQuery(id+"F0.imprint","IMPRINT",FACE,{"disambiguationData":[TD([[makeQuery(id+"F0.imprint","IMPRINT",EDGE,{"disambiguationData":[TD([[subQ2,-1.0]])],"derivedFrom":subQ1}),-1.0]])]});}
            var Q23;
            {var subQ0=sQuery(id+"F0.wireOp",EDGE,"E21.9.0");var subQ1=sQuery(id+"F0.wireOp",EDGE,"E3");var subQ2=makeQuery(id+"F0.imprint","INTERSECT",VERTEX,{"derivedFrom":[subQ1,subQ0]});Q23=makeQuery(id+"F0.imprint","IMPRINT",FACE,{"disambiguationData":[TD([[makeQuery(id+"F0.imprint","IMPRINT",EDGE,{"disambiguationData":[TD([[subQ2,-1.0]])],"derivedFrom":subQ1}),-1.0]])]});}
            extrude(context, id + "F2", {"entities" : qUnion([Q0, Q1, Q2, Q3, Q4, Q5, Q6, Q7, Q8, Q9, Q10, Q11, Q12, Q13, Q14, Q15, Q16, Q17, Q18, Q19, Q20, Q21, Q22, Q23]), "depth" : 5.5 * mm, "hasSecondDirection" : true, "secondDirectionOppositeDirection" : false, "secondDirectionDepth" : 5 * mm});
        }
        {
            var Q0;
            {var subQ3=sQuery(id+"F0.wireOp",EDGE,"E3");var subQ7=sQuery(id+"F0.wireOp",EDGE,"E45");var subQ9=makeQuery(id+"F0.imprint","INTERSECT",VERTEX,{"derivedFrom":[subQ3,subQ7]});Q0=makeQuery(id+"F0.imprint","IMPRINT",FACE,{"disambiguationData":[TD([[makeQuery(id+"F0.imprint","IMPRINT",EDGE,{"disambiguationData":[TD([[subQ9,-1.0]])],"derivedFrom":subQ3}),-1.0]])]});}
            var Q1;
            {var subQ0=sQuery(id+"F0.wireOp",EDGE,"E16");var subQ3=sQuery(id+"F0.wireOp",EDGE,"E3");var subQ4=makeQuery(id+"F0.imprint","INTERSECT",VERTEX,{"derivedFrom":[subQ3,subQ0]});Q1=makeQuery(id+"F0.imprint","IMPRINT",FACE,{"disambiguationData":[TD([[makeQuery(id+"F0.imprint","IMPRINT",EDGE,{"disambiguationData":[TD([[subQ4,-1.0]])],"derivedFrom":subQ3}),-1.0]])]});}
            var Q2;
            {var subQ0=sQuery(id+"F0.wireOp",EDGE,"E21.11.0");var subQ1=sQuery(id+"F0.wireOp",EDGE,"E3");var subQ2=makeQuery(id+"F0.imprint","INTERSECT",VERTEX,{"derivedFrom":[subQ1,subQ0]});Q2=makeQuery(id+"F0.imprint","IMPRINT",FACE,{"disambiguationData":[TD([[makeQuery(id+"F0.imprint","IMPRINT",EDGE,{"disambiguationData":[TD([[subQ2,-1.0]])],"derivedFrom":subQ1}),-1.0]])]});}
            var Q3;
            {var subQ0=sQuery(id+"F0.wireOp",EDGE,"E47.11.0");var subQ1=sQuery(id+"F0.wireOp",EDGE,"E3");var subQ2=makeQuery(id+"F0.imprint","INTERSECT",VERTEX,{"derivedFrom":[subQ1,subQ0]});Q3=makeQuery(id+"F0.imprint","IMPRINT",FACE,{"disambiguationData":[TD([[makeQuery(id+"F0.imprint","IMPRINT",EDGE,{"disambiguationData":[TD([[subQ2,-1.0]])],"derivedFrom":subQ1}),-1.0]])]});}
            var Q4;
            {var subQ0=sQuery(id+"F0.wireOp",EDGE,"E21.10.0");var subQ1=sQuery(id+"F0.wireOp",EDGE,"E3");var subQ2=makeQuery(id+"F0.imprint","INTERSECT",VERTEX,{"derivedFrom":[subQ1,subQ0]});Q4=makeQuery(id+"F0.imprint","IMPRINT",FACE,{"disambiguationData":[TD([[makeQuery(id+"F0.imprint","IMPRINT",EDGE,{"disambiguationData":[TD([[subQ2,-1.0]])],"derivedFrom":subQ1}),-1.0]])]});}
            var Q5;
            {var subQ0=sQuery(id+"F0.wireOp",EDGE,"E47.10.0");var subQ1=sQuery(id+"F0.wireOp",EDGE,"E3");var subQ2=makeQuery(id+"F0.imprint","INTERSECT",VERTEX,{"derivedFrom":[subQ1,subQ0]});Q5=makeQuery(id+"F0.imprint","IMPRINT",FACE,{"disambiguationData":[TD([[makeQuery(id+"F0.imprint","IMPRINT",EDGE,{"disambiguationData":[TD([[subQ2,-1.0]])],"derivedFrom":subQ1}),-1.0]])]});}
            var Q6;
            {var subQ0=sQuery(id+"F0.wireOp",EDGE,"E21.9.0");var subQ1=sQuery(id+"F0.wireOp",EDGE,"E3");var subQ2=makeQuery(id+"F0.imprint","INTERSECT",VERTEX,{"derivedFrom":[subQ1,subQ0]});Q6=makeQuery(id+"F0.imprint","IMPRINT",FACE,{"disambiguationData":[TD([[makeQuery(id+"F0.imprint","IMPRINT",EDGE,{"disambiguationData":[TD([[subQ2,-1.0]])],"derivedFrom":subQ1}),-1.0]])]});}
            var Q7;
            {var subQ0=sQuery(id+"F0.wireOp",EDGE,"E47.9.0");var subQ1=sQuery(id+"F0.wireOp",EDGE,"E3");var subQ2=makeQuery(id+"F0.imprint","INTERSECT",VERTEX,{"derivedFrom":[subQ1,subQ0]});Q7=makeQuery(id+"F0.imprint","IMPRINT",FACE,{"disambiguationData":[TD([[makeQuery(id+"F0.imprint","IMPRINT",EDGE,{"disambiguationData":[TD([[subQ2,-1.0]])],"derivedFrom":subQ1}),-1.0]])]});}
            var Q8;
            {var subQ0=sQuery(id+"F0.wireOp",EDGE,"E47.1.0");var subQ1=sQuery(id+"F0.wireOp",EDGE,"E3");var subQ2=makeQuery(id+"F0.imprint","INTERSECT",VERTEX,{"derivedFrom":[subQ1,subQ0]});Q8=makeQuery(id+"F0.imprint","IMPRINT",FACE,{"disambiguationData":[TD([[makeQuery(id+"F0.imprint","IMPRINT",EDGE,{"disambiguationData":[TD([[subQ2,-1.0]])],"derivedFrom":subQ1}),-1.0]])]});}
            var Q9;
            {var subQ0=sQuery(id+"F0.wireOp",EDGE,"E21.1.0");var subQ1=sQuery(id+"F0.wireOp",EDGE,"E3");var subQ2=makeQuery(id+"F0.imprint","INTERSECT",VERTEX,{"derivedFrom":[subQ1,subQ0]});Q9=makeQuery(id+"F0.imprint","IMPRINT",FACE,{"disambiguationData":[TD([[makeQuery(id+"F0.imprint","IMPRINT",EDGE,{"disambiguationData":[TD([[subQ2,-1.0]])],"derivedFrom":subQ1}),-1.0]])]});}
            var Q10;
            {var subQ0=sQuery(id+"F0.wireOp",EDGE,"E47.2.0");var subQ1=sQuery(id+"F0.wireOp",EDGE,"E3");var subQ2=makeQuery(id+"F0.imprint","INTERSECT",VERTEX,{"derivedFrom":[subQ1,subQ0]});Q10=makeQuery(id+"F0.imprint","IMPRINT",FACE,{"disambiguationData":[TD([[makeQuery(id+"F0.imprint","IMPRINT",EDGE,{"disambiguationData":[TD([[subQ2,-1.0]])],"derivedFrom":subQ1}),-1.0]])]});}
            var Q11;
            {var subQ0=sQuery(id+"F0.wireOp",EDGE,"E21.2.0");var subQ1=sQuery(id+"F0.wireOp",EDGE,"E3");var subQ2=makeQuery(id+"F0.imprint","INTERSECT",VERTEX,{"derivedFrom":[subQ1,subQ0]});Q11=makeQuery(id+"F0.imprint","IMPRINT",FACE,{"disambiguationData":[TD([[makeQuery(id+"F0.imprint","IMPRINT",EDGE,{"disambiguationData":[TD([[subQ2,-1.0]])],"derivedFrom":subQ1}),-1.0]])]});}
            var Q12;
            {var subQ0=sQuery(id+"F0.wireOp",EDGE,"E47.3.0");var subQ1=sQuery(id+"F0.wireOp",EDGE,"E3");var subQ2=makeQuery(id+"F0.imprint","INTERSECT",VERTEX,{"derivedFrom":[subQ1,subQ0]});Q12=makeQuery(id+"F0.imprint","IMPRINT",FACE,{"disambiguationData":[TD([[makeQuery(id+"F0.imprint","IMPRINT",EDGE,{"disambiguationData":[TD([[subQ2,-1.0]])],"derivedFrom":subQ1}),-1.0]])]});}
            var Q13;
            {var subQ0=sQuery(id+"F0.wireOp",EDGE,"E21.3.0");var subQ1=sQuery(id+"F0.wireOp",EDGE,"E3");var subQ2=makeQuery(id+"F0.imprint","INTERSECT",VERTEX,{"derivedFrom":[subQ1,subQ0]});Q13=makeQuery(id+"F0.imprint","IMPRINT",FACE,{"disambiguationData":[TD([[makeQuery(id+"F0.imprint","IMPRINT",EDGE,{"disambiguationData":[TD([[subQ2,-1.0]])],"derivedFrom":subQ1}),-1.0]])]});}
            var Q14;
            {var subQ0=sQuery(id+"F0.wireOp",EDGE,"E21.8.0");var subQ1=sQuery(id+"F0.wireOp",EDGE,"E3");var subQ2=makeQuery(id+"F0.imprint","INTERSECT",VERTEX,{"derivedFrom":[subQ1,subQ0]});Q14=makeQuery(id+"F0.imprint","IMPRINT",FACE,{"disambiguationData":[TD([[makeQuery(id+"F0.imprint","IMPRINT",EDGE,{"disambiguationData":[TD([[subQ2,-1.0]])],"derivedFrom":subQ1}),-1.0]])]});}
            var Q15;
            {var subQ0=sQuery(id+"F0.wireOp",EDGE,"E47.8.0");var subQ1=sQuery(id+"F0.wireOp",EDGE,"E3");var subQ2=makeQuery(id+"F0.imprint","INTERSECT",VERTEX,{"derivedFrom":[subQ1,subQ0]});Q15=makeQuery(id+"F0.imprint","IMPRINT",FACE,{"disambiguationData":[TD([[makeQuery(id+"F0.imprint","IMPRINT",EDGE,{"disambiguationData":[TD([[subQ2,-1.0]])],"derivedFrom":subQ1}),-1.0]])]});}
            var Q16;
            {var subQ0=sQuery(id+"F0.wireOp",EDGE,"E21.7.0");var subQ1=sQuery(id+"F0.wireOp",EDGE,"E3");var subQ2=makeQuery(id+"F0.imprint","INTERSECT",VERTEX,{"derivedFrom":[subQ1,subQ0]});Q16=makeQuery(id+"F0.imprint","IMPRINT",FACE,{"disambiguationData":[TD([[makeQuery(id+"F0.imprint","IMPRINT",EDGE,{"disambiguationData":[TD([[subQ2,-1.0]])],"derivedFrom":subQ1}),-1.0]])]});}
            var Q17;
            {var subQ0=sQuery(id+"F0.wireOp",EDGE,"E47.7.0");var subQ1=sQuery(id+"F0.wireOp",EDGE,"E3");var subQ2=makeQuery(id+"F0.imprint","INTERSECT",VERTEX,{"derivedFrom":[subQ1,subQ0]});Q17=makeQuery(id+"F0.imprint","IMPRINT",FACE,{"disambiguationData":[TD([[makeQuery(id+"F0.imprint","IMPRINT",EDGE,{"disambiguationData":[TD([[subQ2,-1.0]])],"derivedFrom":subQ1}),-1.0]])]});}
            var Q18;
            {var subQ0=sQuery(id+"F0.wireOp",EDGE,"E21.6.0");var subQ1=sQuery(id+"F0.wireOp",EDGE,"E3");var subQ2=makeQuery(id+"F0.imprint","INTERSECT",VERTEX,{"derivedFrom":[subQ1,subQ0]});Q18=makeQuery(id+"F0.imprint","IMPRINT",FACE,{"disambiguationData":[TD([[makeQuery(id+"F0.imprint","IMPRINT",EDGE,{"disambiguationData":[TD([[subQ2,-1.0]])],"derivedFrom":subQ1}),-1.0]])]});}
            var Q19;
            {var subQ0=sQuery(id+"F0.wireOp",EDGE,"E47.6.0");var subQ1=sQuery(id+"F0.wireOp",EDGE,"E3");var subQ2=makeQuery(id+"F0.imprint","INTERSECT",VERTEX,{"derivedFrom":[subQ1,subQ0]});Q19=makeQuery(id+"F0.imprint","IMPRINT",FACE,{"disambiguationData":[TD([[makeQuery(id+"F0.imprint","IMPRINT",EDGE,{"disambiguationData":[TD([[subQ2,-1.0]])],"derivedFrom":subQ1}),-1.0]])]});}
            var Q20;
            {var subQ0=sQuery(id+"F0.wireOp",EDGE,"E21.5.0");var subQ1=sQuery(id+"F0.wireOp",EDGE,"E3");var subQ2=makeQuery(id+"F0.imprint","INTERSECT",VERTEX,{"derivedFrom":[subQ1,subQ0]});Q20=makeQuery(id+"F0.imprint","IMPRINT",FACE,{"disambiguationData":[TD([[makeQuery(id+"F0.imprint","IMPRINT",EDGE,{"disambiguationData":[TD([[subQ2,-1.0]])],"derivedFrom":subQ1}),-1.0]])]});}
            var Q21;
            {var subQ0=sQuery(id+"F0.wireOp",EDGE,"E47.5.0");var subQ1=sQuery(id+"F0.wireOp",EDGE,"E3");var subQ2=makeQuery(id+"F0.imprint","INTERSECT",VERTEX,{"derivedFrom":[subQ1,subQ0]});Q21=makeQuery(id+"F0.imprint","IMPRINT",FACE,{"disambiguationData":[TD([[makeQuery(id+"F0.imprint","IMPRINT",EDGE,{"disambiguationData":[TD([[subQ2,-1.0]])],"derivedFrom":subQ1}),-1.0]])]});}
            var Q22;
            {var subQ0=sQuery(id+"F0.wireOp",EDGE,"E21.4.0");var subQ1=sQuery(id+"F0.wireOp",EDGE,"E3");var subQ2=makeQuery(id+"F0.imprint","INTERSECT",VERTEX,{"derivedFrom":[subQ1,subQ0]});Q22=makeQuery(id+"F0.imprint","IMPRINT",FACE,{"disambiguationData":[TD([[makeQuery(id+"F0.imprint","IMPRINT",EDGE,{"disambiguationData":[TD([[subQ2,-1.0]])],"derivedFrom":subQ1}),-1.0]])]});}
            var Q23;
            {var subQ0=sQuery(id+"F0.wireOp",EDGE,"E47.4.0");var subQ1=sQuery(id+"F0.wireOp",EDGE,"E3");var subQ2=makeQuery(id+"F0.imprint","INTERSECT",VERTEX,{"derivedFrom":[subQ1,subQ0]});Q23=makeQuery(id+"F0.imprint","IMPRINT",FACE,{"disambiguationData":[TD([[makeQuery(id+"F0.imprint","IMPRINT",EDGE,{"disambiguationData":[TD([[subQ2,-1.0]])],"derivedFrom":subQ1}),-1.0]])]});}
            extrude(context, id + "F3", {"entities" : qUnion([Q0, Q1, Q2, Q3, Q4, Q5, Q6, Q7, Q8, Q9, Q10, Q11, Q12, Q13, Q14, Q15, Q16, Q17, Q18, Q19, Q20, Q21, Q22, Q23]), "oppositeDirection" : true, "depth" : .5 * mm, "hasSecondDirection" : true, "secondDirectionOppositeDirection" : true, "secondDirectionDepth" : 0 * mm});
        }
        {
            var Q0;
            {var subQ0=sQuery(id+"F0.wireOp",EDGE,"E20");var subQ1=sQuery(id+"F0.wireOp",EDGE,"E3");var subQ2=makeQuery(id+"F0.imprint","INTERSECT",VERTEX,{"derivedFrom":[subQ1,subQ0]});Q0=makeQuery(id+"F0.imprint","IMPRINT",FACE,{"disambiguationData":[TD([[makeQuery(id+"F0.imprint","IMPRINT",EDGE,{"disambiguationData":[TD([[subQ2,-1.0]])],"derivedFrom":subQ1}),-1.0]])]});}
            var Q1;
            {var subQ0=sQuery(id+"F0.wireOp",EDGE,"E46");var subQ1=sQuery(id+"F0.wireOp",EDGE,"E3");var subQ2=makeQuery(id+"F0.imprint","INTERSECT",VERTEX,{"derivedFrom":[subQ1,subQ0]});Q1=makeQuery(id+"F0.imprint","IMPRINT",FACE,{"disambiguationData":[TD([[makeQuery(id+"F0.imprint","IMPRINT",EDGE,{"disambiguationData":[TD([[subQ2,-1.0]])],"derivedFrom":subQ1}),-1.0]])]});}
            var Q2;
            {var subQ0=sQuery(id+"F0.wireOp",EDGE,"E21.11.5");var subQ1=sQuery(id+"F0.wireOp",EDGE,"E3");var subQ2=makeQuery(id+"F0.imprint","INTERSECT",VERTEX,{"derivedFrom":[subQ1,subQ0]});Q2=makeQuery(id+"F0.imprint","IMPRINT",FACE,{"disambiguationData":[TD([[makeQuery(id+"F0.imprint","IMPRINT",EDGE,{"disambiguationData":[TD([[subQ2,-1.0]])],"derivedFrom":subQ1}),-1.0]])]});}
            var Q3;
            {var subQ0=sQuery(id+"F0.wireOp",EDGE,"E47.11.1");var subQ1=sQuery(id+"F0.wireOp",EDGE,"E3");var subQ2=makeQuery(id+"F0.imprint","INTERSECT",VERTEX,{"derivedFrom":[subQ1,subQ0]});Q3=makeQuery(id+"F0.imprint","IMPRINT",FACE,{"disambiguationData":[TD([[makeQuery(id+"F0.imprint","IMPRINT",EDGE,{"disambiguationData":[TD([[subQ2,-1.0]])],"derivedFrom":subQ1}),-1.0]])]});}
            var Q4;
            {var subQ0=sQuery(id+"F0.wireOp",EDGE,"E47.10.1");var subQ1=sQuery(id+"F0.wireOp",EDGE,"E3");var subQ2=makeQuery(id+"F0.imprint","INTERSECT",VERTEX,{"derivedFrom":[subQ1,subQ0]});Q4=makeQuery(id+"F0.imprint","IMPRINT",FACE,{"disambiguationData":[TD([[makeQuery(id+"F0.imprint","IMPRINT",EDGE,{"disambiguationData":[TD([[subQ2,-1.0]])],"derivedFrom":subQ1}),-1.0]])]});}
            var Q5;
            {var subQ0=sQuery(id+"F0.wireOp",EDGE,"E21.10.5");var subQ1=sQuery(id+"F0.wireOp",EDGE,"E3");var subQ2=makeQuery(id+"F0.imprint","INTERSECT",VERTEX,{"derivedFrom":[subQ1,subQ0]});Q5=makeQuery(id+"F0.imprint","IMPRINT",FACE,{"disambiguationData":[TD([[makeQuery(id+"F0.imprint","IMPRINT",EDGE,{"disambiguationData":[TD([[subQ2,-1.0]])],"derivedFrom":subQ1}),-1.0]])]});}
            var Q6;
            {var subQ0=sQuery(id+"F0.wireOp",EDGE,"E47.9.1");var subQ1=sQuery(id+"F0.wireOp",EDGE,"E3");var subQ2=makeQuery(id+"F0.imprint","INTERSECT",VERTEX,{"derivedFrom":[subQ1,subQ0]});Q6=makeQuery(id+"F0.imprint","IMPRINT",FACE,{"disambiguationData":[TD([[makeQuery(id+"F0.imprint","IMPRINT",EDGE,{"disambiguationData":[TD([[subQ2,-1.0]])],"derivedFrom":subQ1}),-1.0]])]});}
            var Q7;
            {var subQ0=sQuery(id+"F0.wireOp",EDGE,"E21.9.5");var subQ1=sQuery(id+"F0.wireOp",EDGE,"E3");var subQ2=makeQuery(id+"F0.imprint","INTERSECT",VERTEX,{"derivedFrom":[subQ1,subQ0]});Q7=makeQuery(id+"F0.imprint","IMPRINT",FACE,{"disambiguationData":[TD([[makeQuery(id+"F0.imprint","IMPRINT",EDGE,{"disambiguationData":[TD([[subQ2,-1.0]])],"derivedFrom":subQ1}),-1.0]])]});}
            var Q8;
            {var subQ0=sQuery(id+"F0.wireOp",EDGE,"E47.8.1");var subQ1=sQuery(id+"F0.wireOp",EDGE,"E3");var subQ2=makeQuery(id+"F0.imprint","INTERSECT",VERTEX,{"derivedFrom":[subQ1,subQ0]});Q8=makeQuery(id+"F0.imprint","IMPRINT",FACE,{"disambiguationData":[TD([[makeQuery(id+"F0.imprint","IMPRINT",EDGE,{"disambiguationData":[TD([[subQ2,-1.0]])],"derivedFrom":subQ1}),-1.0]])]});}
            var Q9;
            {var subQ0=sQuery(id+"F0.wireOp",EDGE,"E21.8.5");var subQ1=sQuery(id+"F0.wireOp",EDGE,"E3");var subQ2=makeQuery(id+"F0.imprint","INTERSECT",VERTEX,{"derivedFrom":[subQ1,subQ0]});Q9=makeQuery(id+"F0.imprint","IMPRINT",FACE,{"disambiguationData":[TD([[makeQuery(id+"F0.imprint","IMPRINT",EDGE,{"disambiguationData":[TD([[subQ2,-1.0]])],"derivedFrom":subQ1}),-1.0]])]});}
            var Q10;
            {var subQ0=sQuery(id+"F0.wireOp",EDGE,"E47.7.1");var subQ1=sQuery(id+"F0.wireOp",EDGE,"E3");var subQ2=makeQuery(id+"F0.imprint","INTERSECT",VERTEX,{"derivedFrom":[subQ1,subQ0]});Q10=makeQuery(id+"F0.imprint","IMPRINT",FACE,{"disambiguationData":[TD([[makeQuery(id+"F0.imprint","IMPRINT",EDGE,{"disambiguationData":[TD([[subQ2,-1.0]])],"derivedFrom":subQ1}),-1.0]])]});}
            var Q11;
            {var subQ0=sQuery(id+"F0.wireOp",EDGE,"E21.7.5");var subQ1=sQuery(id+"F0.wireOp",EDGE,"E3");var subQ2=makeQuery(id+"F0.imprint","INTERSECT",VERTEX,{"derivedFrom":[subQ1,subQ0]});Q11=makeQuery(id+"F0.imprint","IMPRINT",FACE,{"disambiguationData":[TD([[makeQuery(id+"F0.imprint","IMPRINT",EDGE,{"disambiguationData":[TD([[subQ2,-1.0]])],"derivedFrom":subQ1}),-1.0]])]});}
            var Q12;
            {var subQ0=sQuery(id+"F0.wireOp",EDGE,"E47.6.1");var subQ1=sQuery(id+"F0.wireOp",EDGE,"E3");var subQ2=makeQuery(id+"F0.imprint","INTERSECT",VERTEX,{"derivedFrom":[subQ1,subQ0]});Q12=makeQuery(id+"F0.imprint","IMPRINT",FACE,{"disambiguationData":[TD([[makeQuery(id+"F0.imprint","IMPRINT",EDGE,{"disambiguationData":[TD([[subQ2,-1.0]])],"derivedFrom":subQ1}),-1.0]])]});}
            var Q13;
            {var subQ0=sQuery(id+"F0.wireOp",EDGE,"E21.6.5");var subQ1=sQuery(id+"F0.wireOp",EDGE,"E3");var subQ2=makeQuery(id+"F0.imprint","INTERSECT",VERTEX,{"derivedFrom":[subQ1,subQ0]});Q13=makeQuery(id+"F0.imprint","IMPRINT",FACE,{"disambiguationData":[TD([[makeQuery(id+"F0.imprint","IMPRINT",EDGE,{"disambiguationData":[TD([[subQ2,-1.0]])],"derivedFrom":subQ1}),-1.0]])]});}
            var Q14;
            {var subQ0=sQuery(id+"F0.wireOp",EDGE,"E47.5.1");var subQ1=sQuery(id+"F0.wireOp",EDGE,"E3");var subQ2=makeQuery(id+"F0.imprint","INTERSECT",VERTEX,{"derivedFrom":[subQ1,subQ0]});Q14=makeQuery(id+"F0.imprint","IMPRINT",FACE,{"disambiguationData":[TD([[makeQuery(id+"F0.imprint","IMPRINT",EDGE,{"disambiguationData":[TD([[subQ2,-1.0]])],"derivedFrom":subQ1}),-1.0]])]});}
            var Q15;
            {var subQ0=sQuery(id+"F0.wireOp",EDGE,"E21.5.5");var subQ1=sQuery(id+"F0.wireOp",EDGE,"E3");var subQ2=makeQuery(id+"F0.imprint","INTERSECT",VERTEX,{"derivedFrom":[subQ1,subQ0]});Q15=makeQuery(id+"F0.imprint","IMPRINT",FACE,{"disambiguationData":[TD([[makeQuery(id+"F0.imprint","IMPRINT",EDGE,{"disambiguationData":[TD([[subQ2,-1.0]])],"derivedFrom":subQ1}),-1.0]])]});}
            var Q16;
            {var subQ0=sQuery(id+"F0.wireOp",EDGE,"E47.4.1");var subQ1=sQuery(id+"F0.wireOp",EDGE,"E3");var subQ2=makeQuery(id+"F0.imprint","INTERSECT",VERTEX,{"derivedFrom":[subQ1,subQ0]});Q16=makeQuery(id+"F0.imprint","IMPRINT",FACE,{"disambiguationData":[TD([[makeQuery(id+"F0.imprint","IMPRINT",EDGE,{"disambiguationData":[TD([[subQ2,-1.0]])],"derivedFrom":subQ1}),-1.0]])]});}
            var Q17;
            {var subQ0=sQuery(id+"F0.wireOp",EDGE,"E21.4.5");var subQ1=sQuery(id+"F0.wireOp",EDGE,"E3");var subQ2=makeQuery(id+"F0.imprint","INTERSECT",VERTEX,{"derivedFrom":[subQ1,subQ0]});Q17=makeQuery(id+"F0.imprint","IMPRINT",FACE,{"disambiguationData":[TD([[makeQuery(id+"F0.imprint","IMPRINT",EDGE,{"disambiguationData":[TD([[subQ2,-1.0]])],"derivedFrom":subQ1}),-1.0]])]});}
            var Q18;
            {var subQ0=sQuery(id+"F0.wireOp",EDGE,"E47.3.1");var subQ1=sQuery(id+"F0.wireOp",EDGE,"E3");var subQ2=makeQuery(id+"F0.imprint","INTERSECT",VERTEX,{"derivedFrom":[subQ1,subQ0]});Q18=makeQuery(id+"F0.imprint","IMPRINT",FACE,{"disambiguationData":[TD([[makeQuery(id+"F0.imprint","IMPRINT",EDGE,{"disambiguationData":[TD([[subQ2,-1.0]])],"derivedFrom":subQ1}),-1.0]])]});}
            var Q19;
            {var subQ0=sQuery(id+"F0.wireOp",EDGE,"E21.3.5");var subQ1=sQuery(id+"F0.wireOp",EDGE,"E3");var subQ2=makeQuery(id+"F0.imprint","INTERSECT",VERTEX,{"derivedFrom":[subQ1,subQ0]});Q19=makeQuery(id+"F0.imprint","IMPRINT",FACE,{"disambiguationData":[TD([[makeQuery(id+"F0.imprint","IMPRINT",EDGE,{"disambiguationData":[TD([[subQ2,-1.0]])],"derivedFrom":subQ1}),-1.0]])]});}
            var Q20;
            {var subQ0=sQuery(id+"F0.wireOp",EDGE,"E21.2.6");var subQ1=sQuery(id+"F0.wireOp",EDGE,"E3");var subQ2=makeQuery(id+"F0.imprint","INTERSECT",VERTEX,{"derivedFrom":[subQ1,subQ0]});Q20=makeQuery(id+"F0.imprint","IMPRINT",FACE,{"disambiguationData":[TD([[makeQuery(id+"F0.imprint","IMPRINT",EDGE,{"disambiguationData":[TD([[subQ2,1.0]])],"derivedFrom":subQ1}),-1.0]])]});}
            var Q21;
            {var subQ0=sQuery(id+"F0.wireOp",EDGE,"E21.2.5");var subQ1=sQuery(id+"F0.wireOp",EDGE,"E3");var subQ2=makeQuery(id+"F0.imprint","INTERSECT",VERTEX,{"derivedFrom":[subQ1,subQ0]});Q21=makeQuery(id+"F0.imprint","IMPRINT",FACE,{"disambiguationData":[TD([[makeQuery(id+"F0.imprint","IMPRINT",EDGE,{"disambiguationData":[TD([[subQ2,-1.0]])],"derivedFrom":subQ1}),-1.0]])]});}
            var Q22;
            {var subQ0=sQuery(id+"F0.wireOp",EDGE,"E47.1.1");var subQ1=sQuery(id+"F0.wireOp",EDGE,"E3");var subQ2=makeQuery(id+"F0.imprint","INTERSECT",VERTEX,{"derivedFrom":[subQ1,subQ0]});Q22=makeQuery(id+"F0.imprint","IMPRINT",FACE,{"disambiguationData":[TD([[makeQuery(id+"F0.imprint","IMPRINT",EDGE,{"disambiguationData":[TD([[subQ2,-1.0]])],"derivedFrom":subQ1}),-1.0]])]});}
            var Q23;
            {var subQ0=sQuery(id+"F0.wireOp",EDGE,"E21.1.5");var subQ1=sQuery(id+"F0.wireOp",EDGE,"E3");var subQ2=makeQuery(id+"F0.imprint","INTERSECT",VERTEX,{"derivedFrom":[subQ1,subQ0]});Q23=makeQuery(id+"F0.imprint","IMPRINT",FACE,{"disambiguationData":[TD([[makeQuery(id+"F0.imprint","IMPRINT",EDGE,{"disambiguationData":[TD([[subQ2,-1.0]])],"derivedFrom":subQ1}),-1.0]])]});}
            extrude(context, id + "F4", {"entities" : qUnion([Q0, Q1, Q2, Q3, Q4, Q5, Q6, Q7, Q8, Q9, Q10, Q11, Q12, Q13, Q14, Q15, Q16, Q17, Q18, Q19, Q20, Q21, Q22, Q23]), "depth" : 5.5 * mm, "hasSecondDirection" : true, "secondDirectionOppositeDirection" : true, "secondDirectionDepth" : .50 * mm});
        }
    });
